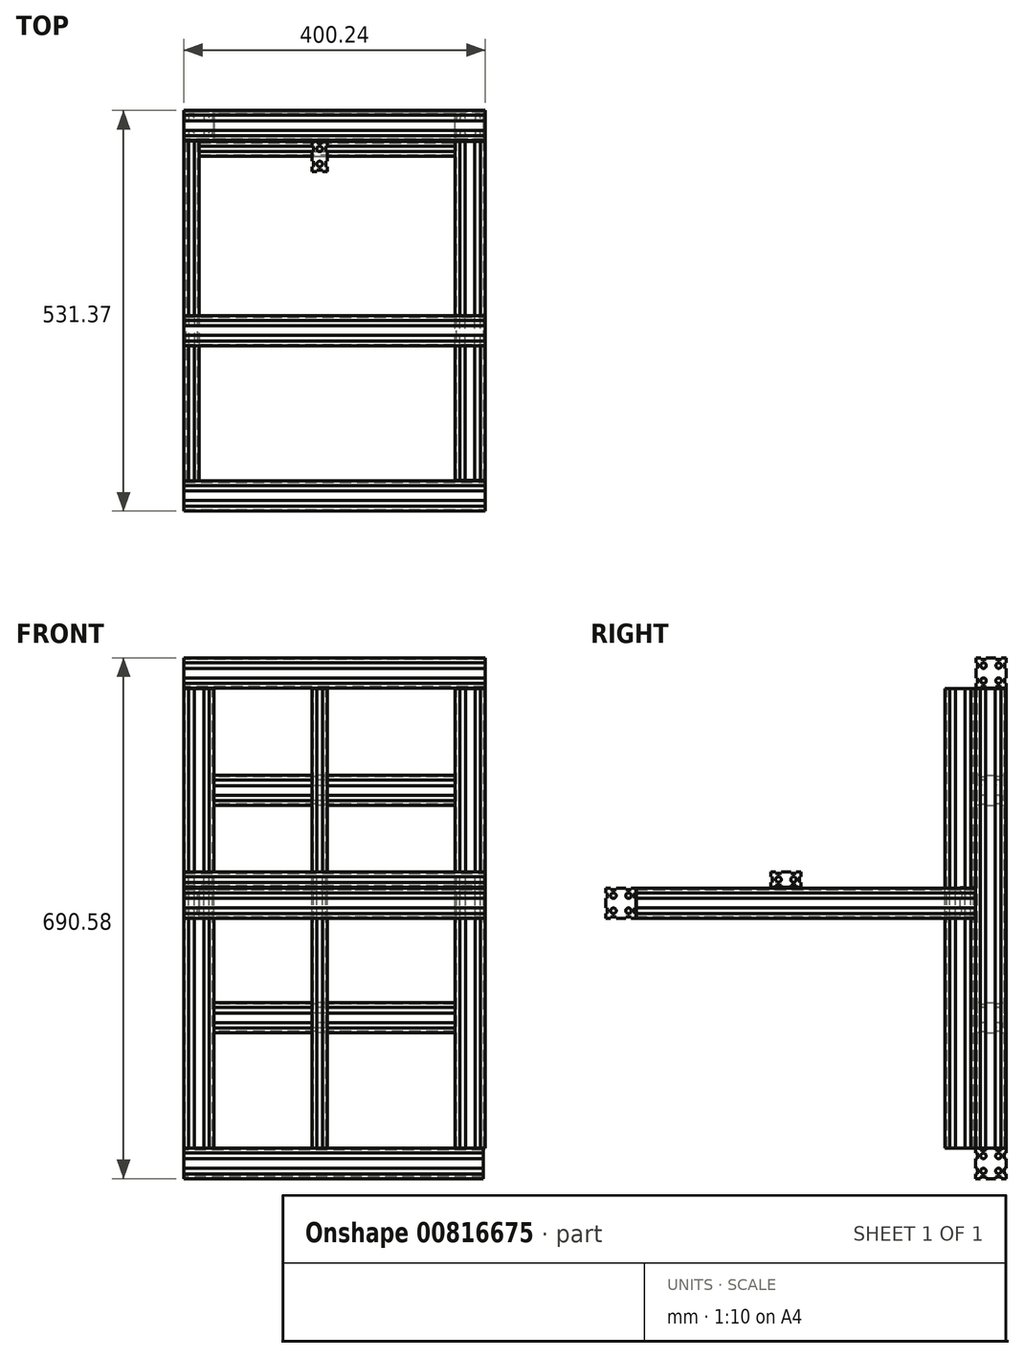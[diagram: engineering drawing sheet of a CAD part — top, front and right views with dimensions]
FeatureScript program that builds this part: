
annotation { "Feature Type Name" : "Feature", "Feature Type Description" : "" }
export const myFeature = defineFeature(function(context is Context, id is Id, definition is map)
    precondition{}
    {
        {
            var Q0;
            Q0=qCreatedBy(makeId("Front.planeOp"),FACE);
            var sketch = newSketch(context, id + "F0", { "sketchPlane" : qUnion([Q0])});
            skLineSegment(sketch, "E0", {"start": v(-13.72, 18.03) * mm, "end": v(-6.35, 18.03) * mm});
            skLineSegment(sketch, "E1", {"start": v(-18.03, 13.72) * mm, "end": v(-18.03, 6.35) * mm});
            skLineSegment(sketch, "E2", {"start": v(-6.35, 20.07) * mm, "end": v(0, 20.07) * mm});
            skLineSegment(sketch, "E3", {"start": v(-13.72, 20.07) * mm, "end": v(-20.07, 20.07) * mm});
            skLineSegment(sketch, "E4", {"start": v(-20.07, 20.07) * mm, "end": v(-20.07, 13.72) * mm});
            skLineSegment(sketch, "E5", {"start": v(-20.07, 6.35) * mm, "end": v(-20.07, 0) * mm});
            skLineSegment(sketch, "E6", {"start": v(-13.72, 18.03) * mm, "end": v(-13.72, 20.07) * mm});
            skLineSegment(sketch, "E7", {"start": v(-6.35, 20.07) * mm, "end": v(-6.35, 18.03) * mm});
            skLineSegment(sketch, "E8", {"start": v(-20.07, 13.72) * mm, "end": v(-18.03, 13.72) * mm});
            skLineSegment(sketch, "E9", {"start": v(-18.03, 6.35) * mm, "end": v(-20.07, 6.35) * mm});
            skLineSegment(sketch, "E10.MirrorCS", {"start": v(6.35, 20.07) * mm, "end": v(0, 20.07) * mm});
            skLineSegment(sketch, "E11.MirrorCS", {"start": v(13.72, 18.03) * mm, "end": v(6.35, 18.03) * mm});
            skLineSegment(sketch, "E12.MirrorCS", {"start": v(13.72, 20.07) * mm, "end": v(20.07, 20.07) * mm});
            skLineSegment(sketch, "E13.MirrorCS", {"start": v(13.72, 18.03) * mm, "end": v(13.72, 20.07) * mm});
            skLineSegment(sketch, "E14.MirrorCS", {"start": v(6.35, 20.07) * mm, "end": v(6.35, 18.03) * mm});
            skLineSegment(sketch, "E15.MirrorCS", {"start": v(20.07, 20.07) * mm, "end": v(20.07, 13.72) * mm});
            skLineSegment(sketch, "E16.MirrorCS", {"start": v(18.03, 13.72) * mm, "end": v(18.03, 6.35) * mm});
            skLineSegment(sketch, "E17.MirrorCS", {"start": v(20.07, 13.72) * mm, "end": v(18.03, 13.72) * mm});
            skLineSegment(sketch, "E18.MirrorCS", {"start": v(18.03, 6.35) * mm, "end": v(20.07, 6.35) * mm});
            skLineSegment(sketch, "E19.MirrorCS", {"start": v(20.07, 6.35) * mm, "end": v(20.07, 0) * mm});
            skCircle(sketch, "E20", {"center": v(-10.03, 10.03) * mm, "radius": 3.68 * mm});
            skPoint(sketch, "E20.centerSnap0", {"position": v(-18.03, 10.03) * mm});
            skPoint(sketch, "E20.centerSnap1", {"position": v(-10.03, 18.03) * mm});
            skCircle(sketch, "E21.MirrorC", {"center": v(10.03, 10.03) * mm, "radius": 3.68 * mm});
            skLineSegment(sketch, "E22.MirrorCS", {"start": v(-6.35, -20.07) * mm, "end": v(-6.35, -18.03) * mm});
            skLineSegment(sketch, "E23.MirrorCS", {"start": v(-13.72, -18.03) * mm, "end": v(-13.72, -20.07) * mm});
            skLineSegment(sketch, "E24.MirrorCS", {"start": v(-18.03, -6.35) * mm, "end": v(-20.07, -6.35) * mm});
            skLineSegment(sketch, "E25.MirrorCS", {"start": v(18.03, -6.35) * mm, "end": v(20.07, -6.35) * mm});
            skLineSegment(sketch, "E26.MirrorCS", {"start": v(-20.07, -13.72) * mm, "end": v(-18.03, -13.72) * mm});
            skLineSegment(sketch, "E27.MirrorCS", {"start": v(6.35, -20.07) * mm, "end": v(6.35, -18.03) * mm});
            skLineSegment(sketch, "E28.MirrorCS", {"start": v(13.72, -18.03) * mm, "end": v(13.72, -20.07) * mm});
            skLineSegment(sketch, "E29.MirrorCS", {"start": v(20.07, -13.72) * mm, "end": v(18.03, -13.72) * mm});
            skLineSegment(sketch, "E30.MirrorCS", {"start": v(-18.03, -13.72) * mm, "end": v(-18.03, -6.35) * mm});
            skLineSegment(sketch, "E31.MirrorCS", {"start": v(-13.72, -18.03) * mm, "end": v(-6.35, -18.03) * mm});
            skLineSegment(sketch, "E32.MirrorCS", {"start": v(18.03, -13.72) * mm, "end": v(18.03, -6.35) * mm});
            skLineSegment(sketch, "E33.MirrorCS", {"start": v(-20.07, -6.35) * mm, "end": v(-20.07, 0) * mm});
            skPoint(sketch, "E34.MirrorP", {"position": v(-18.03, -10.03) * mm});
            skLineSegment(sketch, "E35.MirrorCS", {"start": v(-20.07, -20.07) * mm, "end": v(-20.07, -13.72) * mm});
            skLineSegment(sketch, "E36.MirrorCS", {"start": v(20.07, -20.07) * mm, "end": v(20.07, -13.72) * mm});
            skLineSegment(sketch, "E37.MirrorCS", {"start": v(13.72, -20.07) * mm, "end": v(20.07, -20.07) * mm});
            skPoint(sketch, "E38.MirrorP", {"position": v(-10.03, -18.03) * mm});
            skLineSegment(sketch, "E39.MirrorCS", {"start": v(-6.35, -20.07) * mm, "end": v(0, -20.07) * mm});
            skCircle(sketch, "E40.MirrorC", {"center": v(-10.03, -10.03) * mm, "radius": 3.68 * mm});
            skLineSegment(sketch, "E41.MirrorCS", {"start": v(20.07, -6.35) * mm, "end": v(20.07, 0) * mm});
            skLineSegment(sketch, "E42.MirrorCS", {"start": v(-13.72, -20.07) * mm, "end": v(-20.07, -20.07) * mm});
            skLineSegment(sketch, "E43.MirrorCS", {"start": v(6.35, -20.07) * mm, "end": v(0, -20.07) * mm});
            skLineSegment(sketch, "E44.MirrorCS", {"start": v(13.72, -18.03) * mm, "end": v(6.35, -18.03) * mm});
            skCircle(sketch, "E45.MirrorC", {"center": v(10.03, -10.03) * mm, "radius": 3.68 * mm});
            skSolve(sketch);
        }
        {
            var Q0;
            Q0=makeQuery(id+"F0.imprint","IMPRINT",FACE,{"disambiguationData":[TD([[makeQuery(id+"F0.imprint","IMPRINT",EDGE,{"derivedFrom":sQuery(id+"F0.wireOp",EDGE,"E0")}),-1.0]])]});
            extrude(context, id + "F1", {"entities" : qUnion([Q0]), "depth" : 450.09 * mm, "offsetDistance" : 25.4 * mm});
        }
        {
            var Q0;
            Q0=makeQuery(id+"F1.opExtrude","SWEPT_FACE",FACE,{"disambiguationData":[OSD([sQuery(id+"F0.wireOp",EDGE,"E19.MirrorCS"),sQuery(id+"F0.wireOp",EDGE,"E41.MirrorCS")])]});
            var sketch = newSketch(context, id + "F2", { "sketchPlane" : qUnion([Q0])});
            skLineSegment(sketch, "E46", {"start": v(-484.07, 17.93) * mm, "end": v(-476.7, 17.93) * mm});
            skLineSegment(sketch, "E47", {"start": v(-488.4, 13.6) * mm, "end": v(-488.4, 6.24) * mm});
            skLineSegment(sketch, "E48", {"start": v(-476.7, 19.96) * mm, "end": v(-470.36, 19.96) * mm});
            skLineSegment(sketch, "E49", {"start": v(-484.07, 19.96) * mm, "end": v(-490.42, 19.96) * mm});
            skLineSegment(sketch, "E50", {"start": v(-490.42, 19.96) * mm, "end": v(-490.42, 13.6) * mm});
            skLineSegment(sketch, "E51", {"start": v(-490.42, 6.24) * mm, "end": v(-490.42, -0.1) * mm});
            skLineSegment(sketch, "E52", {"start": v(-484.07, 17.93) * mm, "end": v(-484.07, 19.96) * mm});
            skLineSegment(sketch, "E53", {"start": v(-476.7, 19.96) * mm, "end": v(-476.7, 17.93) * mm});
            skLineSegment(sketch, "E54", {"start": v(-490.42, 13.6) * mm, "end": v(-488.4, 13.6) * mm});
            skLineSegment(sketch, "E55", {"start": v(-488.4, 6.24) * mm, "end": v(-490.42, 6.24) * mm});
            skLineSegment(sketch, "E56.MirrorCS", {"start": v(-464, 19.96) * mm, "end": v(-470.36, 19.96) * mm});
            skLineSegment(sketch, "E57.MirrorCS", {"start": v(-456.64, 17.93) * mm, "end": v(-464, 17.93) * mm});
            skLineSegment(sketch, "E58.MirrorCS", {"start": v(-456.64, 19.96) * mm, "end": v(-450.3, 19.96) * mm});
            skLineSegment(sketch, "E59.MirrorCS", {"start": v(-456.64, 17.93) * mm, "end": v(-456.64, 19.96) * mm});
            skLineSegment(sketch, "E60.MirrorCS", {"start": v(-464, 19.96) * mm, "end": v(-464, 17.93) * mm});
            skLineSegment(sketch, "E61.MirrorCS", {"start": v(-450.3, 19.96) * mm, "end": v(-450.3, 13.6) * mm});
            skLineSegment(sketch, "E62.MirrorCS", {"start": v(-452.32, 13.6) * mm, "end": v(-452.32, 6.24) * mm});
            skLineSegment(sketch, "E63.MirrorCS", {"start": v(-450.3, 13.6) * mm, "end": v(-452.32, 13.6) * mm});
            skLineSegment(sketch, "E64.MirrorCS", {"start": v(-452.32, 6.24) * mm, "end": v(-450.3, 6.24) * mm});
            skLineSegment(sketch, "E65.MirrorCS", {"start": v(-450.3, 6.24) * mm, "end": v(-450.3, -0.1) * mm});
            skCircle(sketch, "E66", {"center": v(-480.39, 9.93) * mm, "radius": 3.68 * mm});
            skPoint(sketch, "E66.centerSnap0", {"position": v(-488.4, 9.93) * mm});
            skPoint(sketch, "E66.centerSnap1", {"position": v(-480.39, 17.93) * mm});
            skCircle(sketch, "E67.MirrorC", {"center": v(-460.32, 9.93) * mm, "radius": 3.68 * mm});
            skLineSegment(sketch, "E68.MirrorCS", {"start": v(-476.7, -20.17) * mm, "end": v(-476.7, -18.14) * mm});
            skLineSegment(sketch, "E69.MirrorCS", {"start": v(-484.07, -18.14) * mm, "end": v(-484.07, -20.17) * mm});
            skLineSegment(sketch, "E70.MirrorCS", {"start": v(-488.4, -6.46) * mm, "end": v(-490.42, -6.46) * mm});
            skLineSegment(sketch, "E71.MirrorCS", {"start": v(-452.32, -6.46) * mm, "end": v(-450.3, -6.46) * mm});
            skLineSegment(sketch, "E72.MirrorCS", {"start": v(-490.42, -13.82) * mm, "end": v(-488.4, -13.82) * mm});
            skLineSegment(sketch, "E73.MirrorCS", {"start": v(-464, -20.17) * mm, "end": v(-464, -18.14) * mm});
            skLineSegment(sketch, "E74.MirrorCS", {"start": v(-456.64, -18.14) * mm, "end": v(-456.64, -20.17) * mm});
            skLineSegment(sketch, "E75.MirrorCS", {"start": v(-450.3, -13.82) * mm, "end": v(-452.32, -13.82) * mm});
            skLineSegment(sketch, "E76.MirrorCS", {"start": v(-488.4, -13.82) * mm, "end": v(-488.4, -6.46) * mm});
            skLineSegment(sketch, "E77.MirrorCS", {"start": v(-484.07, -18.14) * mm, "end": v(-476.7, -18.14) * mm});
            skLineSegment(sketch, "E78.MirrorCS", {"start": v(-452.32, -13.82) * mm, "end": v(-452.32, -6.46) * mm});
            skLineSegment(sketch, "E79.MirrorCS", {"start": v(-490.42, -6.46) * mm, "end": v(-490.42, -0.1) * mm});
            skPoint(sketch, "E80.MirrorP", {"position": v(-488.4, -10.14) * mm});
            skLineSegment(sketch, "E81.MirrorCS", {"start": v(-490.42, -20.17) * mm, "end": v(-490.42, -13.82) * mm});
            skLineSegment(sketch, "E82.MirrorCS", {"start": v(-450.3, -20.17) * mm, "end": v(-450.3, -13.82) * mm});
            skLineSegment(sketch, "E83.MirrorCS", {"start": v(-456.64, -20.17) * mm, "end": v(-450.3, -20.17) * mm});
            skPoint(sketch, "E84.MirrorP", {"position": v(-480.39, -18.14) * mm});
            skLineSegment(sketch, "E85.MirrorCS", {"start": v(-476.7, -20.17) * mm, "end": v(-470.36, -20.17) * mm});
            skCircle(sketch, "E86.MirrorC", {"center": v(-480.39, -10.14) * mm, "radius": 3.68 * mm});
            skLineSegment(sketch, "E87.MirrorCS", {"start": v(-450.3, -6.46) * mm, "end": v(-450.3, -0.1) * mm});
            skLineSegment(sketch, "E88.MirrorCS", {"start": v(-484.07, -20.17) * mm, "end": v(-490.42, -20.17) * mm});
            skLineSegment(sketch, "E89.MirrorCS", {"start": v(-464, -20.17) * mm, "end": v(-470.36, -20.17) * mm});
            skLineSegment(sketch, "E90.MirrorCS", {"start": v(-456.64, -18.14) * mm, "end": v(-464, -18.14) * mm});
            skCircle(sketch, "E91.MirrorC", {"center": v(-460.32, -10.14) * mm, "radius": 3.68 * mm});
            skSolve(sketch);
        }
        {
            var Q0;
            Q0=makeQuery(id+"F2.imprint","IMPRINT",FACE,{"disambiguationData":[TD([[makeQuery(id+"F2.imprint","IMPRINT",EDGE,{"derivedFrom":sQuery(id+"F2.wireOp",EDGE,"E46")}),-1.0]])]});
            extrude(context, id + "F3", {"entities" : qUnion([Q0]), "oppositeDirection" : true, "depth" : 400.05 * mm, "offsetDistance" : 25.4 * mm});
        }
        {
            var Q0;
            Q0=makeQuery(id+"F3.opExtrude","SWEPT_FACE",FACE,{"disambiguationData":[OSD([sQuery(id+"F2.wireOp",EDGE,"E65.MirrorCS"),sQuery(id+"F2.wireOp",EDGE,"E87.MirrorCS")])]});
            var sketch = newSketch(context, id + "F4", { "sketchPlane" : qUnion([Q0])});
            skLineSegment(sketch, "E92", {"start": v(366.24, 17.95) * mm, "end": v(373.6, 17.95) * mm});
            skLineSegment(sketch, "E93", {"start": v(361.92, 13.63) * mm, "end": v(361.92, 6.27) * mm});
            skLineSegment(sketch, "E94", {"start": v(373.6, 19.98) * mm, "end": v(379.95, 19.98) * mm});
            skLineSegment(sketch, "E95", {"start": v(366.24, 19.98) * mm, "end": v(359.89, 19.98) * mm});
            skLineSegment(sketch, "E96", {"start": v(359.89, 19.98) * mm, "end": v(359.89, 13.63) * mm});
            skLineSegment(sketch, "E97", {"start": v(359.89, 6.27) * mm, "end": v(359.89, -0.08) * mm});
            skLineSegment(sketch, "E98", {"start": v(366.24, 17.95) * mm, "end": v(366.24, 19.98) * mm});
            skLineSegment(sketch, "E99", {"start": v(373.6, 19.98) * mm, "end": v(373.6, 17.95) * mm});
            skLineSegment(sketch, "E100", {"start": v(359.89, 13.63) * mm, "end": v(361.92, 13.63) * mm});
            skLineSegment(sketch, "E101", {"start": v(361.92, 6.27) * mm, "end": v(359.89, 6.27) * mm});
            skLineSegment(sketch, "E102.MirrorCS", {"start": v(386.3, 19.98) * mm, "end": v(379.95, 19.98) * mm});
            skLineSegment(sketch, "E103.MirrorCS", {"start": v(393.67, 17.95) * mm, "end": v(386.3, 17.95) * mm});
            skLineSegment(sketch, "E104.MirrorCS", {"start": v(393.67, 19.98) * mm, "end": v(400.02, 19.98) * mm});
            skLineSegment(sketch, "E105.MirrorCS", {"start": v(393.67, 17.95) * mm, "end": v(393.67, 19.98) * mm});
            skLineSegment(sketch, "E106.MirrorCS", {"start": v(386.3, 19.98) * mm, "end": v(386.3, 17.95) * mm});
            skLineSegment(sketch, "E107.MirrorCS", {"start": v(400.02, 19.98) * mm, "end": v(400.02, 13.63) * mm});
            skLineSegment(sketch, "E108.MirrorCS", {"start": v(397.99, 13.63) * mm, "end": v(397.99, 6.27) * mm});
            skLineSegment(sketch, "E109.MirrorCS", {"start": v(400.02, 13.63) * mm, "end": v(397.99, 13.63) * mm});
            skLineSegment(sketch, "E110.MirrorCS", {"start": v(397.99, 6.27) * mm, "end": v(400.02, 6.27) * mm});
            skLineSegment(sketch, "E111.MirrorCS", {"start": v(400.02, 6.27) * mm, "end": v(400.02, -0.08) * mm});
            skCircle(sketch, "E112", {"center": v(369.92, 9.95) * mm, "radius": 3.68 * mm});
            skPoint(sketch, "E112.centerSnap0", {"position": v(361.92, 9.95) * mm});
            skPoint(sketch, "E112.centerSnap1", {"position": v(369.92, 17.95) * mm});
            skCircle(sketch, "E113.MirrorC", {"center": v(389.99, 9.95) * mm, "radius": 3.68 * mm});
            skLineSegment(sketch, "E114.MirrorCS", {"start": v(373.6, -20.15) * mm, "end": v(373.6, -18.12) * mm});
            skLineSegment(sketch, "E115.MirrorCS", {"start": v(366.24, -18.12) * mm, "end": v(366.24, -20.15) * mm});
            skLineSegment(sketch, "E116.MirrorCS", {"start": v(361.92, -6.43) * mm, "end": v(359.89, -6.43) * mm});
            skLineSegment(sketch, "E117.MirrorCS", {"start": v(397.99, -6.43) * mm, "end": v(400.02, -6.43) * mm});
            skLineSegment(sketch, "E118.MirrorCS", {"start": v(359.89, -13.8) * mm, "end": v(361.92, -13.8) * mm});
            skLineSegment(sketch, "E119.MirrorCS", {"start": v(386.3, -20.15) * mm, "end": v(386.3, -18.12) * mm});
            skLineSegment(sketch, "E120.MirrorCS", {"start": v(393.67, -18.12) * mm, "end": v(393.67, -20.15) * mm});
            skLineSegment(sketch, "E121.MirrorCS", {"start": v(400.02, -13.8) * mm, "end": v(397.99, -13.8) * mm});
            skLineSegment(sketch, "E122.MirrorCS", {"start": v(361.92, -13.8) * mm, "end": v(361.92, -6.43) * mm});
            skLineSegment(sketch, "E123.MirrorCS", {"start": v(366.24, -18.12) * mm, "end": v(373.6, -18.12) * mm});
            skLineSegment(sketch, "E124.MirrorCS", {"start": v(397.99, -13.8) * mm, "end": v(397.99, -6.43) * mm});
            skLineSegment(sketch, "E125.MirrorCS", {"start": v(359.89, -6.43) * mm, "end": v(359.89, -0.08) * mm});
            skPoint(sketch, "E126.MirrorP", {"position": v(361.92, -10.11) * mm});
            skLineSegment(sketch, "E127.MirrorCS", {"start": v(359.89, -20.15) * mm, "end": v(359.89, -13.8) * mm});
            skLineSegment(sketch, "E128.MirrorCS", {"start": v(400.02, -20.15) * mm, "end": v(400.02, -13.8) * mm});
            skLineSegment(sketch, "E129.MirrorCS", {"start": v(393.67, -20.15) * mm, "end": v(400.02, -20.15) * mm});
            skPoint(sketch, "E130.MirrorP", {"position": v(369.92, -18.12) * mm});
            skLineSegment(sketch, "E131.MirrorCS", {"start": v(373.6, -20.15) * mm, "end": v(379.95, -20.15) * mm});
            skCircle(sketch, "E132.MirrorC", {"center": v(369.92, -10.11) * mm, "radius": 3.68 * mm});
            skLineSegment(sketch, "E133.MirrorCS", {"start": v(400.02, -6.43) * mm, "end": v(400.02, -0.08) * mm});
            skLineSegment(sketch, "E134.MirrorCS", {"start": v(366.24, -20.15) * mm, "end": v(359.89, -20.15) * mm});
            skLineSegment(sketch, "E135.MirrorCS", {"start": v(386.3, -20.15) * mm, "end": v(379.95, -20.15) * mm});
            skLineSegment(sketch, "E136.MirrorCS", {"start": v(393.67, -18.12) * mm, "end": v(386.3, -18.12) * mm});
            skCircle(sketch, "E137.MirrorC", {"center": v(389.99, -10.11) * mm, "radius": 3.68 * mm});
            skLineSegment(sketch, "E138", {"start": v(379.95, 19.98) * mm, "end": v(379.95, 13.55) * mm});
            skLineSegment(sketch, "E139", {"start": v(379.95, 13.55) * mm, "end": v(377.33, 13.55) * mm});
            skLineSegment(sketch, "E140", {"start": v(377.33, 13.55) * mm, "end": v(377.33, 6.24) * mm});
            skLineSegment(sketch, "E141", {"start": v(377.33, 6.24) * mm, "end": v(379.98, 6.24) * mm});
            skLineSegment(sketch, "E142", {"start": v(379.98, 6.24) * mm, "end": v(379.98, -6.46) * mm});
            skLineSegment(sketch, "E143", {"start": v(379.98, -6.46) * mm, "end": v(377.33, -6.46) * mm});
            skLineSegment(sketch, "E144", {"start": v(377.33, -6.46) * mm, "end": v(377.33, -13.79) * mm});
            skLineSegment(sketch, "E145", {"start": v(377.33, -13.79) * mm, "end": v(379.98, -13.79) * mm});
            skLineSegment(sketch, "E146", {"start": v(379.98, -13.79) * mm, "end": v(379.95, -20.15) * mm});
            skSolve(sketch);
        }
        {
            var Q0;
            Q0=makeQuery(id+"F4.imprint","IMPRINT",FACE,{"disambiguationData":[TD([[makeQuery(id+"F4.imprint","IMPRINT",EDGE,{"derivedFrom":sQuery(id+"F4.wireOp",EDGE,"E92")}),-1.0]])]});
            var Q1;
            {var subQ10=sQuery(id+"F4.wireOp",EDGE,"E116.MirrorCS");Q1=makeQuery(id+"F4.imprint","IMPRINT",FACE,{"disambiguationData":[TD([[makeQuery(id+"F4.imprint","IMPRINT",EDGE,{"derivedFrom":subQ10}),-1.0]])]});}
            var Q2;
            Q2=makeQuery(id+"F4.imprint","IMPRINT",FACE,{"disambiguationData":[TD([[makeQuery(id+"F4.imprint","IMPRINT",EDGE,{"derivedFrom":sQuery(id+"F4.wireOp",EDGE,"E114.MirrorCS")}),-1.0]])]});
            extrude(context, id + "F5", {"entities" : qUnion([Q0, Q1, Q2]), "depth" : 450.85 * mm, "offsetDistance" : 25.4 * mm});
        }
        {
            var Q0;
            Q0=makeQuery(id+"F1.opExtrude","SWEPT_FACE",FACE,{"disambiguationData":[OSD([sQuery(id+"F0.wireOp",EDGE,"E5"),sQuery(id+"F0.wireOp",EDGE,"E33.MirrorCS")])]});
            var sketch = newSketch(context, id + "F6", { "sketchPlane" : qUnion([Q0])});
            skLineSegment(sketch, "E147", {"start": v(-13.72, 18.18) * mm, "end": v(-6.36, 18.18) * mm});
            skLineSegment(sketch, "E148", {"start": v(-18.04, 13.86) * mm, "end": v(-18.04, 6.5) * mm});
            skLineSegment(sketch, "E149", {"start": v(-6.36, 20.21) * mm, "end": v(0, 20.21) * mm});
            skLineSegment(sketch, "E150", {"start": v(-13.72, 20.21) * mm, "end": v(-20.07, 20.21) * mm});
            skLineSegment(sketch, "E151", {"start": v(-20.07, 20.21) * mm, "end": v(-20.07, 13.86) * mm});
            skLineSegment(sketch, "E152", {"start": v(-20.07, 6.5) * mm, "end": v(-20.07, 0.14) * mm});
            skLineSegment(sketch, "E153", {"start": v(-13.72, 18.18) * mm, "end": v(-13.72, 20.21) * mm});
            skLineSegment(sketch, "E154", {"start": v(-6.36, 20.21) * mm, "end": v(-6.36, 18.18) * mm});
            skLineSegment(sketch, "E155", {"start": v(-20.07, 13.86) * mm, "end": v(-18.04, 13.86) * mm});
            skLineSegment(sketch, "E156", {"start": v(-18.04, 6.5) * mm, "end": v(-20.07, 6.5) * mm});
            skLineSegment(sketch, "E157.MirrorCS", {"start": v(6.34, 20.21) * mm, "end": v(0, 20.21) * mm});
            skLineSegment(sketch, "E158.MirrorCS", {"start": v(13.7, 18.18) * mm, "end": v(6.34, 18.18) * mm});
            skLineSegment(sketch, "E159.MirrorCS", {"start": v(13.7, 20.21) * mm, "end": v(20.06, 20.21) * mm});
            skLineSegment(sketch, "E160.MirrorCS", {"start": v(13.7, 18.18) * mm, "end": v(13.7, 20.21) * mm});
            skLineSegment(sketch, "E161.MirrorCS", {"start": v(6.34, 20.21) * mm, "end": v(6.34, 18.18) * mm});
            skLineSegment(sketch, "E162.MirrorCS", {"start": v(20.06, 20.21) * mm, "end": v(20.06, 13.86) * mm});
            skLineSegment(sketch, "E163.MirrorCS", {"start": v(18.03, 13.86) * mm, "end": v(18.03, 6.5) * mm});
            skLineSegment(sketch, "E164.MirrorCS", {"start": v(20.06, 13.86) * mm, "end": v(18.03, 13.86) * mm});
            skLineSegment(sketch, "E165.MirrorCS", {"start": v(18.03, 6.5) * mm, "end": v(20.06, 6.5) * mm});
            skLineSegment(sketch, "E166.MirrorCS", {"start": v(20.06, 6.5) * mm, "end": v(20.06, 0.14) * mm});
            skCircle(sketch, "E167", {"center": v(-10.04, 10.18) * mm, "radius": 3.68 * mm});
            skPoint(sketch, "E167.centerSnap0", {"position": v(-18.04, 10.18) * mm});
            skPoint(sketch, "E167.centerSnap1", {"position": v(-10.04, 18.18) * mm});
            skCircle(sketch, "E168.MirrorC", {"center": v(10.03, 10.18) * mm, "radius": 3.68 * mm});
            skLineSegment(sketch, "E169.MirrorCS", {"start": v(-6.36, -19.92) * mm, "end": v(-6.36, -17.89) * mm});
            skLineSegment(sketch, "E170.MirrorCS", {"start": v(-13.72, -17.89) * mm, "end": v(-13.72, -19.92) * mm});
            skLineSegment(sketch, "E171.MirrorCS", {"start": v(-18.04, -6.2) * mm, "end": v(-20.07, -6.2) * mm});
            skLineSegment(sketch, "E172.MirrorCS", {"start": v(18.03, -6.2) * mm, "end": v(20.06, -6.2) * mm});
            skLineSegment(sketch, "E173.MirrorCS", {"start": v(-20.07, -13.57) * mm, "end": v(-18.04, -13.57) * mm});
            skLineSegment(sketch, "E174.MirrorCS", {"start": v(6.34, -19.92) * mm, "end": v(6.34, -17.89) * mm});
            skLineSegment(sketch, "E175.MirrorCS", {"start": v(13.7, -17.89) * mm, "end": v(13.7, -19.92) * mm});
            skLineSegment(sketch, "E176.MirrorCS", {"start": v(20.06, -13.57) * mm, "end": v(18.03, -13.57) * mm});
            skLineSegment(sketch, "E177.MirrorCS", {"start": v(-18.04, -13.57) * mm, "end": v(-18.04, -6.2) * mm});
            skLineSegment(sketch, "E178.MirrorCS", {"start": v(-13.72, -17.89) * mm, "end": v(-6.36, -17.89) * mm});
            skLineSegment(sketch, "E179.MirrorCS", {"start": v(18.03, -13.57) * mm, "end": v(18.03, -6.2) * mm});
            skLineSegment(sketch, "E180.MirrorCS", {"start": v(-20.07, -6.2) * mm, "end": v(-20.07, 0.14) * mm});
            skPoint(sketch, "E181.MirrorP", {"position": v(-18.04, -9.89) * mm});
            skLineSegment(sketch, "E182.MirrorCS", {"start": v(-20.07, -19.92) * mm, "end": v(-20.07, -13.57) * mm});
            skLineSegment(sketch, "E183.MirrorCS", {"start": v(20.06, -19.92) * mm, "end": v(20.06, -13.57) * mm});
            skLineSegment(sketch, "E184.MirrorCS", {"start": v(13.7, -19.92) * mm, "end": v(20.06, -19.92) * mm});
            skPoint(sketch, "E185.MirrorP", {"position": v(-10.04, -17.89) * mm});
            skLineSegment(sketch, "E186.MirrorCS", {"start": v(-6.36, -19.92) * mm, "end": v(0, -19.92) * mm});
            skCircle(sketch, "E187.MirrorC", {"center": v(-10.04, -9.89) * mm, "radius": 3.68 * mm});
            skLineSegment(sketch, "E188.MirrorCS", {"start": v(20.06, -6.2) * mm, "end": v(20.06, 0.14) * mm});
            skLineSegment(sketch, "E189.MirrorCS", {"start": v(-13.72, -19.92) * mm, "end": v(-20.07, -19.92) * mm});
            skLineSegment(sketch, "E190.MirrorCS", {"start": v(6.34, -19.92) * mm, "end": v(0, -19.92) * mm});
            skLineSegment(sketch, "E191.MirrorCS", {"start": v(13.7, -17.89) * mm, "end": v(6.34, -17.89) * mm});
            skCircle(sketch, "E192.MirrorC", {"center": v(10.03, -9.89) * mm, "radius": 3.68 * mm});
            skLineSegment(sketch, "E193", {"start": v(0, 20.21) * mm, "end": v(0, 13.86) * mm});
            skLineSegment(sketch, "E194", {"start": v(0, 13.86) * mm, "end": v(2.4, 13.86) * mm});
            skLineSegment(sketch, "E195", {"start": v(2.4, 13.86) * mm, "end": v(2.4, 6.35) * mm});
            skLineSegment(sketch, "E196", {"start": v(2.4, 6.35) * mm, "end": v(0, 6.38) * mm});
            skLineSegment(sketch, "E197", {"start": v(0, 6.38) * mm, "end": v(0, -6.35) * mm});
            skLineSegment(sketch, "E198", {"start": v(0, -6.35) * mm, "end": v(2.4, -6.35) * mm});
            skLineSegment(sketch, "E199", {"start": v(2.4, -6.35) * mm, "end": v(2.4, -13.57) * mm});
            skLineSegment(sketch, "E200", {"start": v(0, -19.92) * mm, "end": v(0, -13.57) * mm});
            skLineSegment(sketch, "E201", {"start": v(0, -13.57) * mm, "end": v(2.4, -13.57) * mm});
            skSolve(sketch);
        }
        {
            var Q0;
            {var subQ8=sQuery(id+"F6.wireOp",EDGE,"E172.MirrorCS");Q0=makeQuery(id+"F6.imprint","IMPRINT",FACE,{"disambiguationData":[TD([[makeQuery(id+"F6.imprint","IMPRINT",EDGE,{"derivedFrom":subQ8}),1.0]])]});}
            var Q1;
            Q1=makeQuery(id+"F6.imprint","IMPRINT",FACE,{"disambiguationData":[TD([[makeQuery(id+"F6.imprint","IMPRINT",EDGE,{"derivedFrom":sQuery(id+"F6.wireOp",EDGE,"E157.MirrorCS")}),1.0]])]});
            var Q2;
            Q2=makeQuery(id+"F6.imprint","IMPRINT",FACE,{"disambiguationData":[TD([[makeQuery(id+"F6.imprint","IMPRINT",EDGE,{"derivedFrom":sQuery(id+"F6.wireOp",EDGE,"E174.MirrorCS")}),1.0]])]});
            extrude(context, id + "F7", {"entities" : qUnion([Q0, Q1, Q2]), "depth" : 339.6 * mm, "offsetDistance" : 25.4 * mm});
        }
        {
            var Q0;
            Q0=makeQuery(id+"F1.opExtrude","SWEPT_FACE",FACE,{"disambiguationData":[OSD([sQuery(id+"F0.wireOp",EDGE,"E39.MirrorCS"),sQuery(id+"F0.wireOp",EDGE,"E43.MirrorCS")])]});
            var sketch = newSketch(context, id + "F8", { "sketchPlane" : qUnion([Q0])});
            skLineSegment(sketch, "E202", {"start": v(-13.54, -2.1) * mm, "end": v(-6.17, -2.1) * mm});
            skLineSegment(sketch, "E203", {"start": v(-17.86, -6.43) * mm, "end": v(-17.86, -13.8) * mm});
            skLineSegment(sketch, "E204", {"start": v(-6.17, -0.08) * mm, "end": v(0.18, -0.08) * mm});
            skLineSegment(sketch, "E205", {"start": v(-13.54, -0.08) * mm, "end": v(-19.89, -0.08) * mm});
            skLineSegment(sketch, "E206", {"start": v(-19.89, -0.08) * mm, "end": v(-19.89, -6.43) * mm});
            skLineSegment(sketch, "E207", {"start": v(-19.89, -13.8) * mm, "end": v(-19.89, -20.14) * mm});
            skLineSegment(sketch, "E208", {"start": v(-13.54, -2.1) * mm, "end": v(-13.54, -0.08) * mm});
            skLineSegment(sketch, "E209", {"start": v(-6.17, -0.08) * mm, "end": v(-6.17, -2.1) * mm});
            skLineSegment(sketch, "E210", {"start": v(-19.89, -6.43) * mm, "end": v(-17.86, -6.43) * mm});
            skLineSegment(sketch, "E211", {"start": v(-17.86, -13.8) * mm, "end": v(-19.89, -13.8) * mm});
            skLineSegment(sketch, "E212.MirrorCS", {"start": v(6.53, -0.08) * mm, "end": v(0.18, -0.08) * mm});
            skLineSegment(sketch, "E213.MirrorCS", {"start": v(13.9, -2.1) * mm, "end": v(6.53, -2.1) * mm});
            skLineSegment(sketch, "E214.MirrorCS", {"start": v(13.9, -0.08) * mm, "end": v(20.24, -0.08) * mm});
            skLineSegment(sketch, "E215.MirrorCS", {"start": v(13.9, -2.1) * mm, "end": v(13.9, -0.08) * mm});
            skLineSegment(sketch, "E216.MirrorCS", {"start": v(6.53, -0.08) * mm, "end": v(6.53, -2.1) * mm});
            skLineSegment(sketch, "E217.MirrorCS", {"start": v(20.24, -0.08) * mm, "end": v(20.24, -6.43) * mm});
            skLineSegment(sketch, "E218.MirrorCS", {"start": v(18.21, -6.43) * mm, "end": v(18.21, -13.8) * mm});
            skLineSegment(sketch, "E219.MirrorCS", {"start": v(20.24, -6.43) * mm, "end": v(18.21, -6.43) * mm});
            skLineSegment(sketch, "E220.MirrorCS", {"start": v(18.21, -13.8) * mm, "end": v(20.24, -13.8) * mm});
            skLineSegment(sketch, "E221.MirrorCS", {"start": v(20.24, -13.8) * mm, "end": v(20.24, -20.14) * mm});
            skCircle(sketch, "E222", {"center": v(-9.86, -10.11) * mm, "radius": 3.68 * mm});
            skPoint(sketch, "E222.centerSnap0", {"position": v(-17.86, -10.11) * mm});
            skPoint(sketch, "E222.centerSnap1", {"position": v(-9.86, -2.1) * mm});
            skCircle(sketch, "E223.MirrorC", {"center": v(10.21, -10.11) * mm, "radius": 3.68 * mm});
            skLineSegment(sketch, "E224.MirrorCS", {"start": v(-6.17, -40.2) * mm, "end": v(-6.17, -38.18) * mm});
            skLineSegment(sketch, "E225.MirrorCS", {"start": v(-13.54, -38.18) * mm, "end": v(-13.54, -40.2) * mm});
            skLineSegment(sketch, "E226.MirrorCS", {"start": v(-17.86, -26.5) * mm, "end": v(-19.89, -26.5) * mm});
            skLineSegment(sketch, "E227.MirrorCS", {"start": v(18.21, -26.5) * mm, "end": v(20.24, -26.5) * mm});
            skLineSegment(sketch, "E228.MirrorCS", {"start": v(-19.89, -33.86) * mm, "end": v(-17.86, -33.86) * mm});
            skLineSegment(sketch, "E229.MirrorCS", {"start": v(6.53, -40.2) * mm, "end": v(6.53, -38.18) * mm});
            skLineSegment(sketch, "E230.MirrorCS", {"start": v(13.9, -38.18) * mm, "end": v(13.9, -40.2) * mm});
            skLineSegment(sketch, "E231.MirrorCS", {"start": v(20.24, -33.86) * mm, "end": v(18.21, -33.86) * mm});
            skLineSegment(sketch, "E232.MirrorCS", {"start": v(-17.86, -33.86) * mm, "end": v(-17.86, -26.5) * mm});
            skLineSegment(sketch, "E233.MirrorCS", {"start": v(-13.54, -38.18) * mm, "end": v(-6.17, -38.18) * mm});
            skLineSegment(sketch, "E234.MirrorCS", {"start": v(18.21, -33.86) * mm, "end": v(18.21, -26.5) * mm});
            skLineSegment(sketch, "E235.MirrorCS", {"start": v(-19.89, -26.5) * mm, "end": v(-19.89, -20.14) * mm});
            skPoint(sketch, "E236.MirrorP", {"position": v(-17.86, -30.18) * mm});
            skLineSegment(sketch, "E237.MirrorCS", {"start": v(-19.89, -40.2) * mm, "end": v(-19.89, -33.86) * mm});
            skLineSegment(sketch, "E238.MirrorCS", {"start": v(20.24, -40.2) * mm, "end": v(20.24, -33.86) * mm});
            skLineSegment(sketch, "E239.MirrorCS", {"start": v(13.9, -40.2) * mm, "end": v(20.24, -40.2) * mm});
            skPoint(sketch, "E240.MirrorP", {"position": v(-9.86, -38.18) * mm});
            skLineSegment(sketch, "E241.MirrorCS", {"start": v(-6.17, -40.2) * mm, "end": v(0.18, -40.2) * mm});
            skCircle(sketch, "E242.MirrorC", {"center": v(-9.86, -30.18) * mm, "radius": 3.68 * mm});
            skLineSegment(sketch, "E243.MirrorCS", {"start": v(20.24, -26.5) * mm, "end": v(20.24, -20.14) * mm});
            skLineSegment(sketch, "E244.MirrorCS", {"start": v(-13.54, -40.2) * mm, "end": v(-19.89, -40.2) * mm});
            skLineSegment(sketch, "E245.MirrorCS", {"start": v(6.53, -40.2) * mm, "end": v(0.18, -40.2) * mm});
            skLineSegment(sketch, "E246.MirrorCS", {"start": v(13.9, -38.18) * mm, "end": v(6.53, -38.18) * mm});
            skCircle(sketch, "E247.MirrorC", {"center": v(10.21, -30.18) * mm, "radius": 3.68 * mm});
            skSolve(sketch);
        }
        {
            var Q0;
            Q0=makeQuery(id+"F8.imprint","IMPRINT",FACE,{"disambiguationData":[TD([[makeQuery(id+"F8.imprint","IMPRINT",EDGE,{"derivedFrom":sQuery(id+"F8.wireOp",EDGE,"E202")}),-1.0]])]});
            extrude(context, id + "F9", {"entities" : qUnion([Q0]), "depth" : 304.8 * mm, "offsetDistance" : 25.4 * mm, "hasSecondDirection" : true, "secondDirectionOppositeDirection" : true, "secondDirectionDepth" : 304.8 * mm});
        }
        {
            var Q0;
            Q0=makeQuery(id+"F5.opExtrude","SWEPT_FACE",FACE,{"disambiguationData":[OSD([sQuery(id+"F4.wireOp",EDGE,"E134.MirrorCS")])]});
            var sketch = newSketch(context, id + "F10", { "sketchPlane" : qUnion([Q0])});
            skLineSegment(sketch, "E248", {"start": v(-373.65, -2.75) * mm, "end": v(-366.28, -2.75) * mm});
            skLineSegment(sketch, "E249", {"start": v(-377.96, -7.07) * mm, "end": v(-377.96, -14.43) * mm});
            skLineSegment(sketch, "E250", {"start": v(-366.28, -0.72) * mm, "end": v(-359.93, -0.72) * mm});
            skLineSegment(sketch, "E251", {"start": v(-373.65, -0.72) * mm, "end": v(-380, -0.72) * mm});
            skLineSegment(sketch, "E252", {"start": v(-380, -0.72) * mm, "end": v(-380, -7.07) * mm});
            skLineSegment(sketch, "E253", {"start": v(-380, -14.43) * mm, "end": v(-380, -20.78) * mm});
            skLineSegment(sketch, "E254", {"start": v(-373.65, -2.75) * mm, "end": v(-373.65, -0.72) * mm});
            skLineSegment(sketch, "E255", {"start": v(-366.28, -0.72) * mm, "end": v(-366.28, -2.75) * mm});
            skLineSegment(sketch, "E256", {"start": v(-380, -7.07) * mm, "end": v(-377.96, -7.07) * mm});
            skLineSegment(sketch, "E257", {"start": v(-377.96, -14.43) * mm, "end": v(-380, -14.43) * mm});
            skLineSegment(sketch, "E258.MirrorCS", {"start": v(-353.58, -0.72) * mm, "end": v(-359.93, -0.72) * mm});
            skLineSegment(sketch, "E259.MirrorCS", {"start": v(-346.21, -2.75) * mm, "end": v(-353.58, -2.75) * mm});
            skLineSegment(sketch, "E260.MirrorCS", {"start": v(-346.21, -0.72) * mm, "end": v(-339.86, -0.72) * mm});
            skLineSegment(sketch, "E261.MirrorCS", {"start": v(-346.21, -2.75) * mm, "end": v(-346.21, -0.72) * mm});
            skLineSegment(sketch, "E262.MirrorCS", {"start": v(-353.58, -0.72) * mm, "end": v(-353.58, -2.75) * mm});
            skLineSegment(sketch, "E263.MirrorCS", {"start": v(-339.86, -0.72) * mm, "end": v(-339.86, -7.07) * mm});
            skLineSegment(sketch, "E264.MirrorCS", {"start": v(-341.9, -7.07) * mm, "end": v(-341.9, -14.43) * mm});
            skLineSegment(sketch, "E265.MirrorCS", {"start": v(-339.86, -7.07) * mm, "end": v(-341.9, -7.07) * mm});
            skLineSegment(sketch, "E266.MirrorCS", {"start": v(-341.9, -14.43) * mm, "end": v(-339.86, -14.43) * mm});
            skLineSegment(sketch, "E267.MirrorCS", {"start": v(-339.86, -14.43) * mm, "end": v(-339.86, -20.78) * mm});
            skCircle(sketch, "E268", {"center": v(-369.96, -10.75) * mm, "radius": 3.68 * mm});
            skPoint(sketch, "E268.centerSnap0", {"position": v(-377.96, -10.75) * mm});
            skPoint(sketch, "E268.centerSnap1", {"position": v(-369.96, -2.75) * mm});
            skCircle(sketch, "E269.MirrorC", {"center": v(-349.9, -10.75) * mm, "radius": 3.68 * mm});
            skLineSegment(sketch, "E270.MirrorCS", {"start": v(-366.28, -40.85) * mm, "end": v(-366.28, -38.82) * mm});
            skLineSegment(sketch, "E271.MirrorCS", {"start": v(-373.65, -38.82) * mm, "end": v(-373.65, -40.85) * mm});
            skLineSegment(sketch, "E272.MirrorCS", {"start": v(-377.96, -27.13) * mm, "end": v(-380, -27.13) * mm});
            skLineSegment(sketch, "E273.MirrorCS", {"start": v(-341.9, -27.13) * mm, "end": v(-339.86, -27.13) * mm});
            skLineSegment(sketch, "E274.MirrorCS", {"start": v(-380, -34.5) * mm, "end": v(-377.96, -34.5) * mm});
            skLineSegment(sketch, "E275.MirrorCS", {"start": v(-353.58, -40.85) * mm, "end": v(-353.58, -38.82) * mm});
            skLineSegment(sketch, "E276.MirrorCS", {"start": v(-346.21, -38.82) * mm, "end": v(-346.21, -40.85) * mm});
            skLineSegment(sketch, "E277.MirrorCS", {"start": v(-339.86, -34.5) * mm, "end": v(-341.9, -34.5) * mm});
            skLineSegment(sketch, "E278.MirrorCS", {"start": v(-377.96, -34.5) * mm, "end": v(-377.96, -27.13) * mm});
            skLineSegment(sketch, "E279.MirrorCS", {"start": v(-373.65, -38.82) * mm, "end": v(-366.28, -38.82) * mm});
            skLineSegment(sketch, "E280.MirrorCS", {"start": v(-341.9, -34.5) * mm, "end": v(-341.9, -27.13) * mm});
            skLineSegment(sketch, "E281.MirrorCS", {"start": v(-380, -27.13) * mm, "end": v(-380, -20.78) * mm});
            skPoint(sketch, "E282.MirrorP", {"position": v(-377.96, -30.82) * mm});
            skLineSegment(sketch, "E283.MirrorCS", {"start": v(-380, -40.85) * mm, "end": v(-380, -34.5) * mm});
            skLineSegment(sketch, "E284.MirrorCS", {"start": v(-339.86, -40.85) * mm, "end": v(-339.86, -34.5) * mm});
            skLineSegment(sketch, "E285.MirrorCS", {"start": v(-346.21, -40.85) * mm, "end": v(-339.86, -40.85) * mm});
            skPoint(sketch, "E286.MirrorP", {"position": v(-369.96, -38.82) * mm});
            skLineSegment(sketch, "E287.MirrorCS", {"start": v(-366.28, -40.85) * mm, "end": v(-359.93, -40.85) * mm});
            skCircle(sketch, "E288.MirrorC", {"center": v(-369.96, -30.82) * mm, "radius": 3.68 * mm});
            skLineSegment(sketch, "E289.MirrorCS", {"start": v(-339.86, -27.13) * mm, "end": v(-339.86, -20.78) * mm});
            skLineSegment(sketch, "E290.MirrorCS", {"start": v(-373.65, -40.85) * mm, "end": v(-380, -40.85) * mm});
            skLineSegment(sketch, "E291.MirrorCS", {"start": v(-353.58, -40.85) * mm, "end": v(-359.93, -40.85) * mm});
            skLineSegment(sketch, "E292.MirrorCS", {"start": v(-346.21, -38.82) * mm, "end": v(-353.58, -38.82) * mm});
            skCircle(sketch, "E293.MirrorC", {"center": v(-349.9, -30.82) * mm, "radius": 3.68 * mm});
            skSolve(sketch);
        }
        {
            var Q0;
            Q0=makeQuery(id+"F10.imprint","IMPRINT",FACE,{"disambiguationData":[TD([[makeQuery(id+"F10.imprint","IMPRINT",EDGE,{"derivedFrom":sQuery(id+"F10.wireOp",EDGE,"E248")}),-1.0]])]});
            extrude(context, id + "F11", {"entities" : qUnion([Q0]), "depth" : 304.8 * mm, "offsetDistance" : 25.4 * mm, "hasSecondDirection" : true, "secondDirectionOppositeDirection" : true, "secondDirectionDepth" : 304.8 * mm});
        }
        {
            var Q0;
            Q0=makeQuery(id+"F11.opExtrude","SWEPT_FACE",FACE,{"disambiguationData":[OSD([sQuery(id+"F10.wireOp",EDGE,"E253"),sQuery(id+"F10.wireOp",EDGE,"E281.MirrorCS")])]});
            var sketch = newSketch(context, id + "F12", { "sketchPlane" : qUnion([Q0])});
            skLineSegment(sketch, "E294", {"start": v(-34.6, 323.16) * mm, "end": v(-27.23, 323.16) * mm});
            skLineSegment(sketch, "E295", {"start": v(-38.92, 318.84) * mm, "end": v(-38.92, 311.47) * mm});
            skLineSegment(sketch, "E296", {"start": v(-27.23, 325.2) * mm, "end": v(-20.88, 325.2) * mm});
            skLineSegment(sketch, "E297", {"start": v(-34.6, 325.2) * mm, "end": v(-40.95, 325.2) * mm});
            skLineSegment(sketch, "E298", {"start": v(-40.95, 325.2) * mm, "end": v(-40.95, 318.84) * mm});
            skLineSegment(sketch, "E299", {"start": v(-40.95, 311.47) * mm, "end": v(-40.95, 305.12) * mm});
            skLineSegment(sketch, "E300", {"start": v(-34.6, 323.16) * mm, "end": v(-34.6, 325.2) * mm});
            skLineSegment(sketch, "E301", {"start": v(-27.23, 325.2) * mm, "end": v(-27.23, 323.16) * mm});
            skLineSegment(sketch, "E302", {"start": v(-40.95, 318.84) * mm, "end": v(-38.92, 318.84) * mm});
            skLineSegment(sketch, "E303", {"start": v(-38.92, 311.47) * mm, "end": v(-40.95, 311.47) * mm});
            skLineSegment(sketch, "E304.MirrorCS", {"start": v(-14.53, 325.2) * mm, "end": v(-20.88, 325.2) * mm});
            skLineSegment(sketch, "E305.MirrorCS", {"start": v(-7.17, 323.16) * mm, "end": v(-14.53, 323.16) * mm});
            skLineSegment(sketch, "E306.MirrorCS", {"start": v(-7.17, 325.2) * mm, "end": v(-0.82, 325.2) * mm});
            skLineSegment(sketch, "E307.MirrorCS", {"start": v(-7.17, 323.16) * mm, "end": v(-7.17, 325.2) * mm});
            skLineSegment(sketch, "E308.MirrorCS", {"start": v(-14.53, 325.2) * mm, "end": v(-14.53, 323.16) * mm});
            skLineSegment(sketch, "E309.MirrorCS", {"start": v(-0.82, 325.2) * mm, "end": v(-0.82, 318.84) * mm});
            skLineSegment(sketch, "E310.MirrorCS", {"start": v(-2.85, 318.84) * mm, "end": v(-2.85, 311.47) * mm});
            skLineSegment(sketch, "E311.MirrorCS", {"start": v(-0.82, 318.84) * mm, "end": v(-2.85, 318.84) * mm});
            skLineSegment(sketch, "E312.MirrorCS", {"start": v(-2.85, 311.47) * mm, "end": v(-0.82, 311.47) * mm});
            skLineSegment(sketch, "E313.MirrorCS", {"start": v(-0.82, 311.47) * mm, "end": v(-0.82, 305.12) * mm});
            skCircle(sketch, "E314", {"center": v(-30.91, 315.16) * mm, "radius": 3.68 * mm});
            skPoint(sketch, "E314.centerSnap0", {"position": v(-38.92, 315.16) * mm});
            skPoint(sketch, "E314.centerSnap1", {"position": v(-30.91, 323.16) * mm});
            skCircle(sketch, "E315.MirrorC", {"center": v(-10.85, 315.16) * mm, "radius": 3.68 * mm});
            skLineSegment(sketch, "E316.MirrorCS", {"start": v(-27.23, 285.06) * mm, "end": v(-27.23, 287.1) * mm});
            skLineSegment(sketch, "E317.MirrorCS", {"start": v(-34.6, 287.1) * mm, "end": v(-34.6, 285.06) * mm});
            skLineSegment(sketch, "E318.MirrorCS", {"start": v(-38.92, 298.77) * mm, "end": v(-40.95, 298.77) * mm});
            skLineSegment(sketch, "E319.MirrorCS", {"start": v(-2.85, 298.77) * mm, "end": v(-0.82, 298.77) * mm});
            skLineSegment(sketch, "E320.MirrorCS", {"start": v(-40.95, 291.4) * mm, "end": v(-38.92, 291.4) * mm});
            skLineSegment(sketch, "E321.MirrorCS", {"start": v(-14.53, 285.06) * mm, "end": v(-14.53, 287.1) * mm});
            skLineSegment(sketch, "E322.MirrorCS", {"start": v(-7.17, 287.1) * mm, "end": v(-7.17, 285.06) * mm});
            skLineSegment(sketch, "E323.MirrorCS", {"start": v(-0.82, 291.4) * mm, "end": v(-2.85, 291.4) * mm});
            skLineSegment(sketch, "E324.MirrorCS", {"start": v(-38.92, 291.4) * mm, "end": v(-38.92, 298.77) * mm});
            skLineSegment(sketch, "E325.MirrorCS", {"start": v(-34.6, 287.1) * mm, "end": v(-27.23, 287.1) * mm});
            skLineSegment(sketch, "E326.MirrorCS", {"start": v(-2.85, 291.4) * mm, "end": v(-2.85, 298.77) * mm});
            skLineSegment(sketch, "E327.MirrorCS", {"start": v(-40.95, 298.77) * mm, "end": v(-40.95, 305.12) * mm});
            skPoint(sketch, "E328.MirrorP", {"position": v(-38.92, 295.1) * mm});
            skLineSegment(sketch, "E329.MirrorCS", {"start": v(-40.95, 285.06) * mm, "end": v(-40.95, 291.4) * mm});
            skLineSegment(sketch, "E330.MirrorCS", {"start": v(-0.82, 285.06) * mm, "end": v(-0.82, 291.4) * mm});
            skLineSegment(sketch, "E331.MirrorCS", {"start": v(-7.17, 285.06) * mm, "end": v(-0.82, 285.06) * mm});
            skPoint(sketch, "E332.MirrorP", {"position": v(-30.91, 287.1) * mm});
            skLineSegment(sketch, "E333.MirrorCS", {"start": v(-27.23, 285.06) * mm, "end": v(-20.88, 285.06) * mm});
            skCircle(sketch, "E334.MirrorC", {"center": v(-30.91, 295.1) * mm, "radius": 3.68 * mm});
            skLineSegment(sketch, "E335.MirrorCS", {"start": v(-0.82, 298.77) * mm, "end": v(-0.82, 305.12) * mm});
            skLineSegment(sketch, "E336.MirrorCS", {"start": v(-34.6, 285.06) * mm, "end": v(-40.95, 285.06) * mm});
            skLineSegment(sketch, "E337.MirrorCS", {"start": v(-14.53, 285.06) * mm, "end": v(-20.88, 285.06) * mm});
            skLineSegment(sketch, "E338.MirrorCS", {"start": v(-7.17, 287.1) * mm, "end": v(-14.53, 287.1) * mm});
            skCircle(sketch, "E339.MirrorC", {"center": v(-10.85, 295.1) * mm, "radius": 3.68 * mm});
            skSolve(sketch);
        }
        {
            var Q0;
            Q0=makeQuery(id+"F12.imprint","IMPRINT",FACE,{"disambiguationData":[TD([[makeQuery(id+"F12.imprint","IMPRINT",EDGE,{"derivedFrom":sQuery(id+"F12.wireOp",EDGE,"E294")}),-1.0]])]});
            extrude(context, id + "F13", {"entities" : qUnion([Q0]), "oppositeDirection" : true, "depth" : 400.05 * mm, "offsetDistance" : 25.4 * mm});
        }
        {
            var Q0;
            Q0=makeQuery(id+"F11.opExtrude","SWEPT_FACE",FACE,{"disambiguationData":[OSD([sQuery(id+"F10.wireOp",EDGE,"E253"),sQuery(id+"F10.wireOp",EDGE,"E281.MirrorCS")])]});
            var sketch = newSketch(context, id + "F14", { "sketchPlane" : qUnion([Q0])});
            skLineSegment(sketch, "E340", {"start": v(-34.36, -327.29) * mm, "end": v(-27, -327.29) * mm});
            skLineSegment(sketch, "E341", {"start": v(-38.68, -331.6) * mm, "end": v(-38.68, -338.97) * mm});
            skLineSegment(sketch, "E342", {"start": v(-27, -325.26) * mm, "end": v(-20.65, -325.26) * mm});
            skLineSegment(sketch, "E343", {"start": v(-34.36, -325.26) * mm, "end": v(-40.71, -325.26) * mm});
            skLineSegment(sketch, "E344", {"start": v(-40.71, -325.26) * mm, "end": v(-40.71, -331.6) * mm});
            skLineSegment(sketch, "E345", {"start": v(-40.71, -338.97) * mm, "end": v(-40.71, -345.32) * mm});
            skLineSegment(sketch, "E346", {"start": v(-34.36, -327.29) * mm, "end": v(-34.36, -325.26) * mm});
            skLineSegment(sketch, "E347", {"start": v(-27, -325.26) * mm, "end": v(-27, -327.29) * mm});
            skLineSegment(sketch, "E348", {"start": v(-40.71, -331.6) * mm, "end": v(-38.68, -331.6) * mm});
            skLineSegment(sketch, "E349", {"start": v(-38.68, -338.97) * mm, "end": v(-40.71, -338.97) * mm});
            skLineSegment(sketch, "E350.MirrorCS", {"start": v(-14.3, -325.26) * mm, "end": v(-20.65, -325.26) * mm});
            skLineSegment(sketch, "E351.MirrorCS", {"start": v(-6.93, -327.29) * mm, "end": v(-14.3, -327.29) * mm});
            skLineSegment(sketch, "E352.MirrorCS", {"start": v(-6.93, -325.26) * mm, "end": v(-0.58, -325.26) * mm});
            skLineSegment(sketch, "E353.MirrorCS", {"start": v(-6.93, -327.29) * mm, "end": v(-6.93, -325.26) * mm});
            skLineSegment(sketch, "E354.MirrorCS", {"start": v(-14.3, -325.26) * mm, "end": v(-14.3, -327.29) * mm});
            skLineSegment(sketch, "E355.MirrorCS", {"start": v(-0.58, -325.26) * mm, "end": v(-0.58, -331.6) * mm});
            skLineSegment(sketch, "E356.MirrorCS", {"start": v(-2.61, -331.6) * mm, "end": v(-2.61, -338.97) * mm});
            skLineSegment(sketch, "E357.MirrorCS", {"start": v(-0.58, -331.6) * mm, "end": v(-2.61, -331.6) * mm});
            skLineSegment(sketch, "E358.MirrorCS", {"start": v(-2.61, -338.97) * mm, "end": v(-0.58, -338.97) * mm});
            skLineSegment(sketch, "E359.MirrorCS", {"start": v(-0.58, -338.97) * mm, "end": v(-0.58, -345.32) * mm});
            skCircle(sketch, "E360", {"center": v(-30.68, -335.29) * mm, "radius": 3.68 * mm});
            skPoint(sketch, "E360.centerSnap0", {"position": v(-38.68, -335.29) * mm});
            skPoint(sketch, "E360.centerSnap1", {"position": v(-30.68, -327.29) * mm});
            skCircle(sketch, "E361.MirrorC", {"center": v(-10.62, -335.29) * mm, "radius": 3.68 * mm});
            skLineSegment(sketch, "E362.MirrorCS", {"start": v(-27, -365.39) * mm, "end": v(-27, -363.36) * mm});
            skLineSegment(sketch, "E363.MirrorCS", {"start": v(-34.36, -363.36) * mm, "end": v(-34.36, -365.39) * mm});
            skLineSegment(sketch, "E364.MirrorCS", {"start": v(-38.68, -351.67) * mm, "end": v(-40.71, -351.67) * mm});
            skLineSegment(sketch, "E365.MirrorCS", {"start": v(-2.61, -351.67) * mm, "end": v(-0.58, -351.67) * mm});
            skLineSegment(sketch, "E366.MirrorCS", {"start": v(-40.71, -359.04) * mm, "end": v(-38.68, -359.04) * mm});
            skLineSegment(sketch, "E367.MirrorCS", {"start": v(-14.3, -365.39) * mm, "end": v(-14.3, -363.36) * mm});
            skLineSegment(sketch, "E368.MirrorCS", {"start": v(-6.93, -363.36) * mm, "end": v(-6.93, -365.39) * mm});
            skLineSegment(sketch, "E369.MirrorCS", {"start": v(-0.58, -359.04) * mm, "end": v(-2.61, -359.04) * mm});
            skLineSegment(sketch, "E370.MirrorCS", {"start": v(-38.68, -359.04) * mm, "end": v(-38.68, -351.67) * mm});
            skLineSegment(sketch, "E371.MirrorCS", {"start": v(-34.36, -363.36) * mm, "end": v(-27, -363.36) * mm});
            skLineSegment(sketch, "E372.MirrorCS", {"start": v(-2.61, -359.04) * mm, "end": v(-2.61, -351.67) * mm});
            skLineSegment(sketch, "E373.MirrorCS", {"start": v(-40.71, -351.67) * mm, "end": v(-40.71, -345.32) * mm});
            skPoint(sketch, "E374.MirrorP", {"position": v(-38.68, -355.35) * mm});
            skLineSegment(sketch, "E375.MirrorCS", {"start": v(-40.71, -365.39) * mm, "end": v(-40.71, -359.04) * mm});
            skLineSegment(sketch, "E376.MirrorCS", {"start": v(-0.58, -365.39) * mm, "end": v(-0.58, -359.04) * mm});
            skLineSegment(sketch, "E377.MirrorCS", {"start": v(-6.93, -365.39) * mm, "end": v(-0.58, -365.39) * mm});
            skPoint(sketch, "E378.MirrorP", {"position": v(-30.68, -363.36) * mm});
            skLineSegment(sketch, "E379.MirrorCS", {"start": v(-27, -365.39) * mm, "end": v(-20.65, -365.39) * mm});
            skCircle(sketch, "E380.MirrorC", {"center": v(-30.68, -355.35) * mm, "radius": 3.68 * mm});
            skLineSegment(sketch, "E381.MirrorCS", {"start": v(-0.58, -351.67) * mm, "end": v(-0.58, -345.32) * mm});
            skLineSegment(sketch, "E382.MirrorCS", {"start": v(-34.36, -365.39) * mm, "end": v(-40.71, -365.39) * mm});
            skLineSegment(sketch, "E383.MirrorCS", {"start": v(-14.3, -365.39) * mm, "end": v(-20.65, -365.39) * mm});
            skLineSegment(sketch, "E384.MirrorCS", {"start": v(-6.93, -363.36) * mm, "end": v(-14.3, -363.36) * mm});
            skCircle(sketch, "E385.MirrorC", {"center": v(-10.62, -355.35) * mm, "radius": 3.68 * mm});
            skSolve(sketch);
        }
        {
            var Q0;
            Q0=makeQuery(id+"F14.imprint","IMPRINT",FACE,{"disambiguationData":[TD([[makeQuery(id+"F14.imprint","IMPRINT",EDGE,{"derivedFrom":sQuery(id+"F14.wireOp",EDGE,"E340")}),-1.0]])]});
            extrude(context, id + "F15", {"entities" : qUnion([Q0]), "oppositeDirection" : true, "depth" : 397.5 * mm, "offsetDistance" : 25.4 * mm});
        }
        {
            var Q0;
            Q0=makeQuery(id+"F7.opExtrude","SWEPT_FACE",FACE,{"disambiguationData":[OSD([sQuery(id+"F6.wireOp",EDGE,"E184.MirrorCS")])]});
            var sketch = newSketch(context, id + "F16", { "sketchPlane" : qUnion([Q0])});
            skLineSegment(sketch, "E386", {"start": v(-203.34, 38.1) * mm, "end": v(-195.98, 38.1) * mm});
            skLineSegment(sketch, "E387", {"start": v(-207.66, 33.78) * mm, "end": v(-207.66, 26.42) * mm});
            skLineSegment(sketch, "E388", {"start": v(-195.98, 40.13) * mm, "end": v(-189.63, 40.13) * mm});
            skLineSegment(sketch, "E389", {"start": v(-203.34, 40.13) * mm, "end": v(-209.7, 40.13) * mm});
            skLineSegment(sketch, "E390", {"start": v(-209.7, 40.13) * mm, "end": v(-209.7, 33.78) * mm});
            skLineSegment(sketch, "E391", {"start": v(-209.7, 26.42) * mm, "end": v(-209.7, 20.07) * mm});
            skLineSegment(sketch, "E392", {"start": v(-203.34, 38.1) * mm, "end": v(-203.34, 40.13) * mm});
            skLineSegment(sketch, "E393", {"start": v(-195.98, 40.13) * mm, "end": v(-195.98, 38.1) * mm});
            skLineSegment(sketch, "E394", {"start": v(-209.7, 33.78) * mm, "end": v(-207.66, 33.78) * mm});
            skLineSegment(sketch, "E395", {"start": v(-207.66, 26.42) * mm, "end": v(-209.7, 26.42) * mm});
            skLineSegment(sketch, "E396.MirrorCS", {"start": v(-183.28, 40.13) * mm, "end": v(-189.63, 40.13) * mm});
            skLineSegment(sketch, "E397.MirrorCS", {"start": v(-175.91, 38.1) * mm, "end": v(-183.28, 38.1) * mm});
            skLineSegment(sketch, "E398.MirrorCS", {"start": v(-175.91, 40.13) * mm, "end": v(-169.56, 40.13) * mm});
            skLineSegment(sketch, "E399.MirrorCS", {"start": v(-175.91, 38.1) * mm, "end": v(-175.91, 40.13) * mm});
            skLineSegment(sketch, "E400.MirrorCS", {"start": v(-183.28, 40.13) * mm, "end": v(-183.28, 38.1) * mm});
            skLineSegment(sketch, "E401.MirrorCS", {"start": v(-169.56, 40.13) * mm, "end": v(-169.56, 33.78) * mm});
            skLineSegment(sketch, "E402.MirrorCS", {"start": v(-171.6, 33.78) * mm, "end": v(-171.6, 26.42) * mm});
            skLineSegment(sketch, "E403.MirrorCS", {"start": v(-169.56, 33.78) * mm, "end": v(-171.6, 33.78) * mm});
            skLineSegment(sketch, "E404.MirrorCS", {"start": v(-171.6, 26.42) * mm, "end": v(-169.56, 26.42) * mm});
            skLineSegment(sketch, "E405.MirrorCS", {"start": v(-169.56, 26.42) * mm, "end": v(-169.56, 20.07) * mm});
            skCircle(sketch, "E406", {"center": v(-199.66, 30.1) * mm, "radius": 3.68 * mm});
            skPoint(sketch, "E406.centerSnap0", {"position": v(-207.66, 30.1) * mm});
            skPoint(sketch, "E406.centerSnap1", {"position": v(-199.66, 38.1) * mm});
            skCircle(sketch, "E407.MirrorC", {"center": v(-179.6, 30.1) * mm, "radius": 3.68 * mm});
            skLineSegment(sketch, "E408.MirrorCS", {"start": v(-195.98, 0) * mm, "end": v(-195.98, 2.03) * mm});
            skLineSegment(sketch, "E409.MirrorCS", {"start": v(-203.34, 2.03) * mm, "end": v(-203.34, 0) * mm});
            skLineSegment(sketch, "E410.MirrorCS", {"start": v(-207.66, 13.72) * mm, "end": v(-209.7, 13.72) * mm});
            skLineSegment(sketch, "E411.MirrorCS", {"start": v(-171.6, 13.72) * mm, "end": v(-169.56, 13.72) * mm});
            skLineSegment(sketch, "E412.MirrorCS", {"start": v(-209.7, 6.35) * mm, "end": v(-207.66, 6.35) * mm});
            skLineSegment(sketch, "E413.MirrorCS", {"start": v(-183.28, 0) * mm, "end": v(-183.28, 2.03) * mm});
            skLineSegment(sketch, "E414.MirrorCS", {"start": v(-175.91, 2.03) * mm, "end": v(-175.91, 0) * mm});
            skLineSegment(sketch, "E415.MirrorCS", {"start": v(-169.56, 6.35) * mm, "end": v(-171.6, 6.35) * mm});
            skLineSegment(sketch, "E416.MirrorCS", {"start": v(-207.66, 6.35) * mm, "end": v(-207.66, 13.72) * mm});
            skLineSegment(sketch, "E417.MirrorCS", {"start": v(-203.34, 2.03) * mm, "end": v(-195.98, 2.03) * mm});
            skLineSegment(sketch, "E418.MirrorCS", {"start": v(-171.6, 6.35) * mm, "end": v(-171.6, 13.72) * mm});
            skLineSegment(sketch, "E419.MirrorCS", {"start": v(-209.7, 13.72) * mm, "end": v(-209.7, 20.07) * mm});
            skPoint(sketch, "E420.MirrorP", {"position": v(-207.66, 10.03) * mm});
            skLineSegment(sketch, "E421.MirrorCS", {"start": v(-209.7, 0) * mm, "end": v(-209.7, 6.35) * mm});
            skLineSegment(sketch, "E422.MirrorCS", {"start": v(-169.56, 0) * mm, "end": v(-169.56, 6.35) * mm});
            skLineSegment(sketch, "E423.MirrorCS", {"start": v(-175.91, 0) * mm, "end": v(-169.56, 0) * mm});
            skPoint(sketch, "E424.MirrorP", {"position": v(-199.66, 2.03) * mm});
            skLineSegment(sketch, "E425.MirrorCS", {"start": v(-195.98, 0) * mm, "end": v(-189.63, 0) * mm});
            skCircle(sketch, "E426.MirrorC", {"center": v(-199.66, 10.03) * mm, "radius": 3.68 * mm});
            skLineSegment(sketch, "E427.MirrorCS", {"start": v(-169.56, 13.72) * mm, "end": v(-169.56, 20.07) * mm});
            skLineSegment(sketch, "E428.MirrorCS", {"start": v(-203.34, 0) * mm, "end": v(-209.7, 0) * mm});
            skLineSegment(sketch, "E429.MirrorCS", {"start": v(-183.28, 0) * mm, "end": v(-189.63, 0) * mm});
            skLineSegment(sketch, "E430.MirrorCS", {"start": v(-175.91, 2.03) * mm, "end": v(-183.28, 2.03) * mm});
            skCircle(sketch, "E431.MirrorC", {"center": v(-179.6, 10.03) * mm, "radius": 3.68 * mm});
            skLineSegment(sketch, "E432", {"start": v(-199.66, 38.1) * mm, "end": v(-199.66, 34.8) * mm});
            skLineSegment(sketch, "E433.MirrorCS", {"start": v(-189.63, 40.13) * mm, "end": v(-189.63, 33.78) * mm});
            skLineSegment(sketch, "E434.MirrorCS", {"start": v(-189.63, 33.78) * mm, "end": v(-191.66, 33.78) * mm});
            skLineSegment(sketch, "E435.MirrorCS", {"start": v(-191.66, 33.78) * mm, "end": v(-191.66, 26.42) * mm});
            skLineSegment(sketch, "E436.MirrorCS", {"start": v(-191.66, 26.42) * mm, "end": v(-189.63, 26.42) * mm});
            skLineSegment(sketch, "E437.MirrorCS", {"start": v(-189.63, 26.42) * mm, "end": v(-189.63, 20.07) * mm});
            skLineSegment(sketch, "E438.MirrorCS", {"start": v(-189.63, 13.72) * mm, "end": v(-189.63, 20.07) * mm});
            skLineSegment(sketch, "E439.MirrorCS", {"start": v(-191.66, 13.72) * mm, "end": v(-189.63, 13.72) * mm});
            skLineSegment(sketch, "E440.MirrorCS", {"start": v(-191.66, 6.35) * mm, "end": v(-191.66, 13.72) * mm});
            skLineSegment(sketch, "E441.MirrorCS", {"start": v(-189.63, 6.35) * mm, "end": v(-191.66, 6.35) * mm});
            skLineSegment(sketch, "E442.MirrorCS", {"start": v(-189.63, 0) * mm, "end": v(-189.63, 6.35) * mm});
            skSolve(sketch);
        }
        {
            var Q0;
            Q0=makeQuery(id+"F16.imprint","IMPRINT",FACE,{"disambiguationData":[TD([[makeQuery(id+"F16.imprint","IMPRINT",EDGE,{"derivedFrom":sQuery(id+"F16.wireOp",EDGE,"E387")}),1.0]])]});
            var Q1;
            {var subQ1=sQuery(id+"F16.wireOp",EDGE,"E410.MirrorCS");Q1=makeQuery(id+"F16.imprint","IMPRINT",FACE,{"disambiguationData":[TD([[makeQuery(id+"F16.imprint","IMPRINT",EDGE,{"derivedFrom":subQ1}),-1.0]])]});}
            var Q2;
            Q2=makeQuery(id+"F16.imprint","IMPRINT",FACE,{"disambiguationData":[TD([[makeQuery(id+"F16.imprint","IMPRINT",EDGE,{"derivedFrom":sQuery(id+"F16.wireOp",EDGE,"E408.MirrorCS")}),-1.0]])]});
            extrude(context, id + "F17", {"entities" : qUnion([Q0, Q1, Q2]), "depth" : 304.8 * mm, "offsetDistance" : 25.4 * mm, "hasSecondDirection" : true, "secondDirectionOppositeDirection" : true, "secondDirectionDepth" : 304.8 * mm});
        }
        {
            var Q0;
            Q0=makeQuery(id+"F1.opExtrude","SWEPT_FACE",FACE,{"disambiguationData":[OSD([sQuery(id+"F0.wireOp",EDGE,"E15.MirrorCS")])]});
            var sketch = newSketch(context, id + "F18", { "sketchPlane" : qUnion([Q0])});
            skLineSegment(sketch, "E443", {"start": v(-265.01, 59.44) * mm, "end": v(-257.65, 59.44) * mm});
            skLineSegment(sketch, "E444", {"start": v(-269.33, 55.12) * mm, "end": v(-269.33, 47.75) * mm});
            skLineSegment(sketch, "E445", {"start": v(-257.65, 61.47) * mm, "end": v(-251.3, 61.47) * mm});
            skLineSegment(sketch, "E446", {"start": v(-265.01, 61.47) * mm, "end": v(-271.36, 61.47) * mm});
            skLineSegment(sketch, "E447", {"start": v(-271.36, 61.47) * mm, "end": v(-271.36, 55.12) * mm});
            skLineSegment(sketch, "E448", {"start": v(-271.36, 47.75) * mm, "end": v(-271.36, 41.4) * mm});
            skLineSegment(sketch, "E449", {"start": v(-265.01, 59.44) * mm, "end": v(-265.01, 61.47) * mm});
            skLineSegment(sketch, "E450", {"start": v(-257.65, 61.47) * mm, "end": v(-257.65, 59.44) * mm});
            skLineSegment(sketch, "E451", {"start": v(-271.36, 55.12) * mm, "end": v(-269.33, 55.12) * mm});
            skLineSegment(sketch, "E452", {"start": v(-269.33, 47.75) * mm, "end": v(-271.36, 47.75) * mm});
            skLineSegment(sketch, "E453.MirrorCS", {"start": v(-244.95, 61.47) * mm, "end": v(-251.3, 61.47) * mm});
            skLineSegment(sketch, "E454.MirrorCS", {"start": v(-237.58, 59.44) * mm, "end": v(-244.95, 59.44) * mm});
            skLineSegment(sketch, "E455.MirrorCS", {"start": v(-237.58, 61.47) * mm, "end": v(-231.23, 61.47) * mm});
            skLineSegment(sketch, "E456.MirrorCS", {"start": v(-237.58, 59.44) * mm, "end": v(-237.58, 61.47) * mm});
            skLineSegment(sketch, "E457.MirrorCS", {"start": v(-244.95, 61.47) * mm, "end": v(-244.95, 59.44) * mm});
            skLineSegment(sketch, "E458.MirrorCS", {"start": v(-231.23, 61.47) * mm, "end": v(-231.23, 55.12) * mm});
            skLineSegment(sketch, "E459.MirrorCS", {"start": v(-233.26, 55.12) * mm, "end": v(-233.26, 47.75) * mm});
            skLineSegment(sketch, "E460.MirrorCS", {"start": v(-231.23, 55.12) * mm, "end": v(-233.26, 55.12) * mm});
            skLineSegment(sketch, "E461.MirrorCS", {"start": v(-233.26, 47.75) * mm, "end": v(-231.23, 47.75) * mm});
            skLineSegment(sketch, "E462.MirrorCS", {"start": v(-231.23, 47.75) * mm, "end": v(-231.23, 41.4) * mm});
            skCircle(sketch, "E463", {"center": v(-261.33, 51.44) * mm, "radius": 3.68 * mm});
            skPoint(sketch, "E463.centerSnap0", {"position": v(-269.33, 51.44) * mm});
            skPoint(sketch, "E463.centerSnap1", {"position": v(-261.33, 59.44) * mm});
            skCircle(sketch, "E464.MirrorC", {"center": v(-241.26, 51.44) * mm, "radius": 3.68 * mm});
            skLineSegment(sketch, "E465.MirrorCS", {"start": v(-257.65, 21.34) * mm, "end": v(-257.65, 23.37) * mm});
            skLineSegment(sketch, "E466.MirrorCS", {"start": v(-265.01, 23.37) * mm, "end": v(-265.01, 21.34) * mm});
            skLineSegment(sketch, "E467.MirrorCS", {"start": v(-269.33, 35.05) * mm, "end": v(-271.36, 35.05) * mm});
            skLineSegment(sketch, "E468.MirrorCS", {"start": v(-233.26, 35.05) * mm, "end": v(-231.23, 35.05) * mm});
            skLineSegment(sketch, "E469.MirrorCS", {"start": v(-271.36, 27.69) * mm, "end": v(-269.33, 27.69) * mm});
            skLineSegment(sketch, "E470.MirrorCS", {"start": v(-244.95, 21.34) * mm, "end": v(-244.95, 23.37) * mm});
            skLineSegment(sketch, "E471.MirrorCS", {"start": v(-237.58, 23.37) * mm, "end": v(-237.58, 21.34) * mm});
            skLineSegment(sketch, "E472.MirrorCS", {"start": v(-231.23, 27.69) * mm, "end": v(-233.26, 27.69) * mm});
            skLineSegment(sketch, "E473.MirrorCS", {"start": v(-269.33, 27.69) * mm, "end": v(-269.33, 35.05) * mm});
            skLineSegment(sketch, "E474.MirrorCS", {"start": v(-265.01, 23.37) * mm, "end": v(-257.65, 23.37) * mm});
            skLineSegment(sketch, "E475.MirrorCS", {"start": v(-233.26, 27.69) * mm, "end": v(-233.26, 35.05) * mm});
            skLineSegment(sketch, "E476.MirrorCS", {"start": v(-271.36, 35.05) * mm, "end": v(-271.36, 41.4) * mm});
            skPoint(sketch, "E477.MirrorP", {"position": v(-269.33, 31.37) * mm});
            skLineSegment(sketch, "E478.MirrorCS", {"start": v(-271.36, 21.34) * mm, "end": v(-271.36, 27.69) * mm});
            skLineSegment(sketch, "E479.MirrorCS", {"start": v(-231.23, 21.34) * mm, "end": v(-231.23, 27.69) * mm});
            skLineSegment(sketch, "E480.MirrorCS", {"start": v(-237.58, 21.34) * mm, "end": v(-231.23, 21.34) * mm});
            skPoint(sketch, "E481.MirrorP", {"position": v(-261.33, 23.37) * mm});
            skLineSegment(sketch, "E482.MirrorCS", {"start": v(-257.65, 21.34) * mm, "end": v(-251.3, 21.34) * mm});
            skCircle(sketch, "E483.MirrorC", {"center": v(-261.33, 31.37) * mm, "radius": 3.68 * mm});
            skLineSegment(sketch, "E484.MirrorCS", {"start": v(-231.23, 35.05) * mm, "end": v(-231.23, 41.4) * mm});
            skLineSegment(sketch, "E485.MirrorCS", {"start": v(-265.01, 21.34) * mm, "end": v(-271.36, 21.34) * mm});
            skLineSegment(sketch, "E486.MirrorCS", {"start": v(-244.95, 21.34) * mm, "end": v(-251.3, 21.34) * mm});
            skLineSegment(sketch, "E487.MirrorCS", {"start": v(-237.58, 23.37) * mm, "end": v(-244.95, 23.37) * mm});
            skCircle(sketch, "E488.MirrorC", {"center": v(-241.26, 31.37) * mm, "radius": 3.68 * mm});
            skLineSegment(sketch, "E489", {"start": v(-269.33, 31.37) * mm, "end": v(-266.64, 31.37) * mm});
            skLineSegment(sketch, "E490.MirrorCS", {"start": v(-257.65, 41.4) * mm, "end": v(-257.65, 39.37) * mm});
            skLineSegment(sketch, "E491.MirrorCS", {"start": v(-237.58, 39.37) * mm, "end": v(-237.58, 41.4) * mm});
            skLineSegment(sketch, "E492.MirrorCS", {"start": v(-265.01, 39.37) * mm, "end": v(-265.01, 41.4) * mm});
            skLineSegment(sketch, "E493.MirrorCS", {"start": v(-244.95, 41.4) * mm, "end": v(-244.95, 39.37) * mm});
            skLineSegment(sketch, "E494.MirrorCS", {"start": v(-265.01, 39.37) * mm, "end": v(-257.65, 39.37) * mm});
            skLineSegment(sketch, "E495.MirrorCS", {"start": v(-244.95, 41.4) * mm, "end": v(-251.3, 41.4) * mm});
            skLineSegment(sketch, "E496.MirrorCS", {"start": v(-271.36, 41.4) * mm, "end": v(-271.36, 35.05) * mm});
            skLineSegment(sketch, "E497.MirrorCS", {"start": v(-265.01, 41.4) * mm, "end": v(-271.36, 41.4) * mm});
            skLineSegment(sketch, "E498.MirrorCS", {"start": v(-257.65, 41.4) * mm, "end": v(-251.3, 41.4) * mm});
            skPoint(sketch, "E499.MirrorP", {"position": v(-261.33, 39.37) * mm});
            skLineSegment(sketch, "E500.MirrorCS", {"start": v(-237.58, 41.4) * mm, "end": v(-231.23, 41.4) * mm});
            skLineSegment(sketch, "E501.MirrorCS", {"start": v(-231.23, 41.4) * mm, "end": v(-231.23, 35.05) * mm});
            skLineSegment(sketch, "E502.MirrorCS", {"start": v(-237.58, 39.37) * mm, "end": v(-244.95, 39.37) * mm});
            skSolve(sketch);
        }
        {
            var Q0;
            Q0=makeQuery(id+"F18.imprint","IMPRINT",FACE,{"disambiguationData":[TD([[makeQuery(id+"F18.imprint","IMPRINT",EDGE,{"derivedFrom":sQuery(id+"F18.wireOp",EDGE,"E465.MirrorCS")}),-1.0]])]});
            extrude(context, id + "F19", {"entities" : qUnion([Q0]), "oppositeDirection" : true, "depth" : 400.05 * mm, "offsetDistance" : 25.4 * mm});
        }
        {
            var Q0;
            Q0=makeQuery(id+"F11.opExtrude","SWEPT_FACE",FACE,{"disambiguationData":[OSD([sQuery(id+"F10.wireOp",EDGE,"E267.MirrorCS"),sQuery(id+"F10.wireOp",EDGE,"E289.MirrorCS")])]});
            var sketch = newSketch(context, id + "F20", { "sketchPlane" : qUnion([Q0])});
            skLineSegment(sketch, "E503", {"start": v(6.35, -133.98) * mm, "end": v(13.72, -133.98) * mm});
            skLineSegment(sketch, "E504", {"start": v(2.03, -138.3) * mm, "end": v(2.03, -145.66) * mm});
            skLineSegment(sketch, "E505", {"start": v(13.72, -131.94) * mm, "end": v(20.07, -131.94) * mm});
            skLineSegment(sketch, "E506", {"start": v(6.35, -131.94) * mm, "end": v(0, -131.94) * mm});
            skLineSegment(sketch, "E507", {"start": v(0, -131.94) * mm, "end": v(0, -138.3) * mm});
            skLineSegment(sketch, "E508", {"start": v(0, -145.66) * mm, "end": v(0, -152.01) * mm});
            skLineSegment(sketch, "E509", {"start": v(6.35, -133.98) * mm, "end": v(6.35, -131.94) * mm});
            skLineSegment(sketch, "E510", {"start": v(13.72, -131.94) * mm, "end": v(13.72, -133.98) * mm});
            skLineSegment(sketch, "E511", {"start": v(0, -138.3) * mm, "end": v(2.03, -138.3) * mm});
            skLineSegment(sketch, "E512", {"start": v(2.03, -145.66) * mm, "end": v(0, -145.66) * mm});
            skLineSegment(sketch, "E513.MirrorCS", {"start": v(26.42, -131.94) * mm, "end": v(20.07, -131.94) * mm});
            skLineSegment(sketch, "E514.MirrorCS", {"start": v(33.78, -133.98) * mm, "end": v(26.42, -133.98) * mm});
            skLineSegment(sketch, "E515.MirrorCS", {"start": v(33.78, -131.94) * mm, "end": v(40.13, -131.94) * mm});
            skLineSegment(sketch, "E516.MirrorCS", {"start": v(33.78, -133.98) * mm, "end": v(33.78, -131.94) * mm});
            skLineSegment(sketch, "E517.MirrorCS", {"start": v(26.42, -131.94) * mm, "end": v(26.42, -133.98) * mm});
            skLineSegment(sketch, "E518.MirrorCS", {"start": v(40.13, -131.94) * mm, "end": v(40.13, -138.3) * mm});
            skLineSegment(sketch, "E519.MirrorCS", {"start": v(38.1, -138.3) * mm, "end": v(38.1, -145.66) * mm});
            skLineSegment(sketch, "E520.MirrorCS", {"start": v(40.13, -138.3) * mm, "end": v(38.1, -138.3) * mm});
            skLineSegment(sketch, "E521.MirrorCS", {"start": v(38.1, -145.66) * mm, "end": v(40.13, -145.66) * mm});
            skLineSegment(sketch, "E522.MirrorCS", {"start": v(40.13, -145.66) * mm, "end": v(40.13, -152.01) * mm});
            skCircle(sketch, "E523", {"center": v(10.03, -141.98) * mm, "radius": 3.68 * mm});
            skPoint(sketch, "E523.centerSnap0", {"position": v(2.03, -141.98) * mm});
            skPoint(sketch, "E523.centerSnap1", {"position": v(10.03, -133.98) * mm});
            skCircle(sketch, "E524.MirrorC", {"center": v(30.1, -141.98) * mm, "radius": 3.68 * mm});
            skLineSegment(sketch, "E525.MirrorCS", {"start": v(13.72, -172.08) * mm, "end": v(13.72, -170.04) * mm});
            skLineSegment(sketch, "E526.MirrorCS", {"start": v(6.35, -170.04) * mm, "end": v(6.35, -172.08) * mm});
            skLineSegment(sketch, "E527.MirrorCS", {"start": v(2.03, -158.36) * mm, "end": v(0, -158.36) * mm});
            skLineSegment(sketch, "E528.MirrorCS", {"start": v(38.1, -158.36) * mm, "end": v(40.13, -158.36) * mm});
            skLineSegment(sketch, "E529.MirrorCS", {"start": v(0, -165.73) * mm, "end": v(2.03, -165.73) * mm});
            skLineSegment(sketch, "E530.MirrorCS", {"start": v(26.42, -172.08) * mm, "end": v(26.42, -170.04) * mm});
            skLineSegment(sketch, "E531.MirrorCS", {"start": v(33.78, -170.04) * mm, "end": v(33.78, -172.08) * mm});
            skLineSegment(sketch, "E532.MirrorCS", {"start": v(40.13, -165.73) * mm, "end": v(38.1, -165.73) * mm});
            skLineSegment(sketch, "E533.MirrorCS", {"start": v(2.03, -165.73) * mm, "end": v(2.03, -158.36) * mm});
            skLineSegment(sketch, "E534.MirrorCS", {"start": v(6.35, -170.04) * mm, "end": v(13.72, -170.04) * mm});
            skLineSegment(sketch, "E535.MirrorCS", {"start": v(38.1, -165.73) * mm, "end": v(38.1, -158.36) * mm});
            skLineSegment(sketch, "E536.MirrorCS", {"start": v(0, -158.36) * mm, "end": v(0, -152.01) * mm});
            skPoint(sketch, "E537.MirrorP", {"position": v(2.03, -162.04) * mm});
            skLineSegment(sketch, "E538.MirrorCS", {"start": v(0, -172.08) * mm, "end": v(0, -165.73) * mm});
            skLineSegment(sketch, "E539.MirrorCS", {"start": v(40.13, -172.08) * mm, "end": v(40.13, -165.73) * mm});
            skLineSegment(sketch, "E540.MirrorCS", {"start": v(33.78, -172.08) * mm, "end": v(40.13, -172.08) * mm});
            skPoint(sketch, "E541.MirrorP", {"position": v(10.03, -170.04) * mm});
            skLineSegment(sketch, "E542.MirrorCS", {"start": v(13.72, -172.08) * mm, "end": v(20.07, -172.08) * mm});
            skCircle(sketch, "E543.MirrorC", {"center": v(10.03, -162.04) * mm, "radius": 3.68 * mm});
            skLineSegment(sketch, "E544.MirrorCS", {"start": v(40.13, -158.36) * mm, "end": v(40.13, -152.01) * mm});
            skLineSegment(sketch, "E545.MirrorCS", {"start": v(6.35, -172.08) * mm, "end": v(0, -172.08) * mm});
            skLineSegment(sketch, "E546.MirrorCS", {"start": v(26.42, -172.08) * mm, "end": v(20.07, -172.08) * mm});
            skLineSegment(sketch, "E547.MirrorCS", {"start": v(33.78, -170.04) * mm, "end": v(26.42, -170.04) * mm});
            skCircle(sketch, "E548.MirrorC", {"center": v(30.1, -162.04) * mm, "radius": 3.68 * mm});
            skSolve(sketch);
        }
        {
            var Q0;
            Q0 = qSketchRegion(id + "F20", true);
            extrude(context, id + "F21", {"entities" : qUnion([Q0]), "depth" : 320.04 * mm, "offsetDistance" : 25.4 * mm});
        }
        {
            var Q0;
            Q0=makeQuery(id+"F11.opExtrude","SWEPT_FACE",FACE,{"disambiguationData":[OSD([sQuery(id+"F10.wireOp",EDGE,"E267.MirrorCS"),sQuery(id+"F10.wireOp",EDGE,"E289.MirrorCS")])]});
            var sketch = newSketch(context, id + "F22", { "sketchPlane" : qUnion([Q0])});
            skLineSegment(sketch, "E549", {"start": v(6.35, 167.6) * mm, "end": v(13.72, 167.6) * mm});
            skLineSegment(sketch, "E550", {"start": v(2.03, 163.27) * mm, "end": v(2.03, 155.9) * mm});
            skLineSegment(sketch, "E551", {"start": v(13.72, 169.62) * mm, "end": v(20.07, 169.62) * mm});
            skLineSegment(sketch, "E552", {"start": v(6.35, 169.62) * mm, "end": v(0, 169.62) * mm});
            skLineSegment(sketch, "E553", {"start": v(0, 169.62) * mm, "end": v(0, 163.27) * mm});
            skLineSegment(sketch, "E554", {"start": v(0, 155.9) * mm, "end": v(0, 149.56) * mm});
            skLineSegment(sketch, "E555", {"start": v(6.35, 167.6) * mm, "end": v(6.35, 169.62) * mm});
            skLineSegment(sketch, "E556", {"start": v(13.72, 169.62) * mm, "end": v(13.72, 167.6) * mm});
            skLineSegment(sketch, "E557", {"start": v(0, 163.27) * mm, "end": v(2.03, 163.27) * mm});
            skLineSegment(sketch, "E558", {"start": v(2.03, 155.9) * mm, "end": v(0, 155.9) * mm});
            skLineSegment(sketch, "E559.MirrorCS", {"start": v(26.42, 169.62) * mm, "end": v(20.07, 169.62) * mm});
            skLineSegment(sketch, "E560.MirrorCS", {"start": v(33.78, 167.6) * mm, "end": v(26.42, 167.6) * mm});
            skLineSegment(sketch, "E561.MirrorCS", {"start": v(33.78, 169.62) * mm, "end": v(40.13, 169.62) * mm});
            skLineSegment(sketch, "E562.MirrorCS", {"start": v(33.78, 167.6) * mm, "end": v(33.78, 169.62) * mm});
            skLineSegment(sketch, "E563.MirrorCS", {"start": v(26.42, 169.62) * mm, "end": v(26.42, 167.6) * mm});
            skLineSegment(sketch, "E564.MirrorCS", {"start": v(40.13, 169.62) * mm, "end": v(40.13, 163.27) * mm});
            skLineSegment(sketch, "E565.MirrorCS", {"start": v(38.1, 163.27) * mm, "end": v(38.1, 155.9) * mm});
            skLineSegment(sketch, "E566.MirrorCS", {"start": v(40.13, 163.27) * mm, "end": v(38.1, 163.27) * mm});
            skLineSegment(sketch, "E567.MirrorCS", {"start": v(38.1, 155.9) * mm, "end": v(40.13, 155.9) * mm});
            skLineSegment(sketch, "E568.MirrorCS", {"start": v(40.13, 155.9) * mm, "end": v(40.13, 149.56) * mm});
            skCircle(sketch, "E569", {"center": v(10.03, 159.6) * mm, "radius": 3.68 * mm});
            skPoint(sketch, "E569.centerSnap0", {"position": v(2.03, 159.6) * mm});
            skPoint(sketch, "E569.centerSnap1", {"position": v(10.03, 167.6) * mm});
            skCircle(sketch, "E570.MirrorC", {"center": v(30.1, 159.6) * mm, "radius": 3.68 * mm});
            skLineSegment(sketch, "E571.MirrorCS", {"start": v(13.72, 129.5) * mm, "end": v(13.72, 131.52) * mm});
            skLineSegment(sketch, "E572.MirrorCS", {"start": v(6.35, 131.52) * mm, "end": v(6.35, 129.5) * mm});
            skLineSegment(sketch, "E573.MirrorCS", {"start": v(2.03, 143.2) * mm, "end": v(0, 143.2) * mm});
            skLineSegment(sketch, "E574.MirrorCS", {"start": v(38.1, 143.2) * mm, "end": v(40.13, 143.2) * mm});
            skLineSegment(sketch, "E575.MirrorCS", {"start": v(0, 135.84) * mm, "end": v(2.03, 135.84) * mm});
            skLineSegment(sketch, "E576.MirrorCS", {"start": v(26.42, 129.5) * mm, "end": v(26.42, 131.52) * mm});
            skLineSegment(sketch, "E577.MirrorCS", {"start": v(33.78, 131.52) * mm, "end": v(33.78, 129.5) * mm});
            skLineSegment(sketch, "E578.MirrorCS", {"start": v(40.13, 135.84) * mm, "end": v(38.1, 135.84) * mm});
            skLineSegment(sketch, "E579.MirrorCS", {"start": v(2.03, 135.84) * mm, "end": v(2.03, 143.2) * mm});
            skLineSegment(sketch, "E580.MirrorCS", {"start": v(6.35, 131.52) * mm, "end": v(13.72, 131.52) * mm});
            skLineSegment(sketch, "E581.MirrorCS", {"start": v(38.1, 135.84) * mm, "end": v(38.1, 143.2) * mm});
            skLineSegment(sketch, "E582.MirrorCS", {"start": v(0, 143.2) * mm, "end": v(0, 149.56) * mm});
            skPoint(sketch, "E583.MirrorP", {"position": v(2.03, 139.52) * mm});
            skLineSegment(sketch, "E584.MirrorCS", {"start": v(0, 129.5) * mm, "end": v(0, 135.84) * mm});
            skLineSegment(sketch, "E585.MirrorCS", {"start": v(40.13, 129.5) * mm, "end": v(40.13, 135.84) * mm});
            skLineSegment(sketch, "E586.MirrorCS", {"start": v(33.78, 129.5) * mm, "end": v(40.13, 129.5) * mm});
            skPoint(sketch, "E587.MirrorP", {"position": v(10.03, 131.52) * mm});
            skLineSegment(sketch, "E588.MirrorCS", {"start": v(13.72, 129.5) * mm, "end": v(20.07, 129.5) * mm});
            skCircle(sketch, "E589.MirrorC", {"center": v(10.03, 139.52) * mm, "radius": 3.68 * mm});
            skLineSegment(sketch, "E590.MirrorCS", {"start": v(40.13, 143.2) * mm, "end": v(40.13, 149.56) * mm});
            skLineSegment(sketch, "E591.MirrorCS", {"start": v(6.35, 129.5) * mm, "end": v(0, 129.5) * mm});
            skLineSegment(sketch, "E592.MirrorCS", {"start": v(26.42, 129.5) * mm, "end": v(20.07, 129.5) * mm});
            skLineSegment(sketch, "E593.MirrorCS", {"start": v(33.78, 131.52) * mm, "end": v(26.42, 131.52) * mm});
            skCircle(sketch, "E594.MirrorC", {"center": v(30.1, 139.52) * mm, "radius": 3.68 * mm});
            skSolve(sketch);
        }
        {
            var Q0;
            Q0 = qSketchRegion(id + "F22", true);
            extrude(context, id + "F23", {"entities" : qUnion([Q0]), "depth" : 320.04 * mm, "offsetDistance" : 25.4 * mm});
        }
    });
